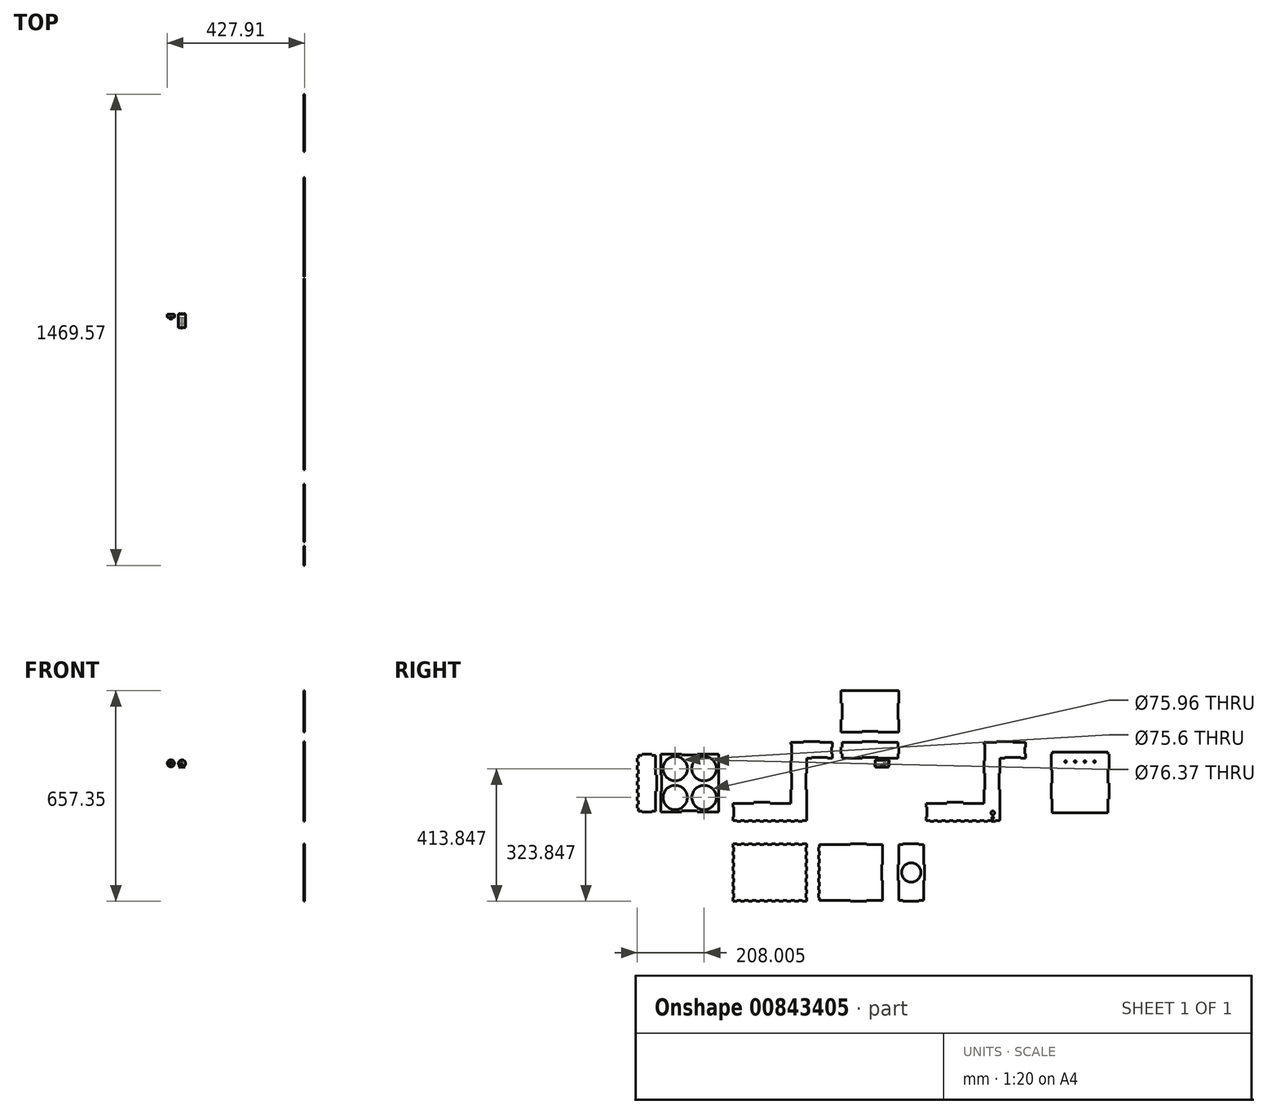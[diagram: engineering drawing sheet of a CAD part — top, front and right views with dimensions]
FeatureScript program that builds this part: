
annotation { "Feature Type Name" : "Feature", "Feature Type Description" : "" }
export const myFeature = defineFeature(function(context is Context, id is Id, definition is map)
    precondition{}
    {
        {
            var Q0;
            Q0=qCreatedBy(makeId("Right.planeOp"),FACE);
            var sketch = newSketch(context, id + "F0", { "sketchPlane" : qUnion([Q0])});
            skLineSegment(sketch, "E0", {"start": v(-485.36, -317) * mm, "end": v(-485.36, -305) * mm});
            skLineSegment(sketch, "E1", {"start": v(-305.36, -263) * mm, "end": v(-370.36, -263) * mm});
            skLineSegment(sketch, "E2", {"start": v(-265.36, -73) * mm, "end": v(-265.36, -70) * mm});
            skLineSegment(sketch, "E3", {"start": v(-265.36, -70) * mm, "end": v(-215.36, -70) * mm});
            skLineSegment(sketch, "E4", {"start": v(-215.36, -70) * mm, "end": v(-215.36, -73) * mm});
            skPoint(sketch, "E5.visualSharp", {"position": v(-175.36, -73) * mm});
            skPoint(sketch, "E6.visualSharp", {"position": v(-175.36, -123) * mm});
            skLineSegment(sketch, "E7", {"start": v(-485.36, -263) * mm, "end": v(-420.36, -263) * mm});
            skLineSegment(sketch, "E8", {"start": v(-420.36, -263) * mm, "end": v(-420.36, -260) * mm});
            skLineSegment(sketch, "E9", {"start": v(-420.36, -260) * mm, "end": v(-370.36, -260) * mm});
            skLineSegment(sketch, "E10", {"start": v(-370.36, -260) * mm, "end": v(-370.36, -263) * mm});
            skLineSegment(sketch, "E11.trimOffspring", {"start": v(-420.36, -263) * mm, "end": v(-485.36, -263) * mm});
            skLineSegment(sketch, "E12", {"start": v(-175.36, -118) * mm, "end": v(-175.36, -123) * mm});
            skLineSegment(sketch, "E13.bottom", {"start": v(-530.36, -290) * mm, "end": v(-595.36, -290) * mm});
            skLineSegment(sketch, "E13.top", {"start": v(-530.36, -110) * mm, "end": v(-595.36, -110) * mm});
            skLineSegment(sketch, "E13.left", {"start": v(-530.36, -290) * mm, "end": v(-530.36, -110) * mm});
            skLineSegment(sketch, "E13.right", {"start": v(-710.36, -290) * mm, "end": v(-710.36, -225) * mm});
            skLineSegment(sketch, "E14", {"start": v(-530.36, -290) * mm, "end": v(-535.36, -290) * mm});
            skLineSegment(sketch, "E15", {"start": v(-589.84, -110) * mm, "end": v(-595.36, -110) * mm});
            skLineSegment(sketch, "E16", {"start": v(-710.36, -110) * mm, "end": v(-705.36, -110) * mm});
            skLineSegment(sketch, "E17", {"start": v(-710.36, -290) * mm, "end": v(-705.36, -290) * mm});
            skLineSegment(sketch, "E18", {"start": v(-710.36, -290) * mm, "end": v(-710.36, -285) * mm});
            skLineSegment(sketch, "E19", {"start": v(-530.36, -110) * mm, "end": v(-530.36, -115) * mm});
            skLineSegment(sketch, "E20", {"start": v(-530.36, -110) * mm, "end": v(-530.36, -200) * mm});
            skCircle(sketch, "E21", {"center": v(-575.36, -245) * mm, "radius": 37.98 * mm});
            skCircle(sketch, "E22", {"center": v(-665.36, -245) * mm, "radius": 37.78 * mm});
            skCircle(sketch, "E23", {"center": v(-665.36, -155) * mm, "radius": 37.8 * mm});
            skCircle(sketch, "E24", {"center": v(-575.36, -155) * mm, "radius": 38.18 * mm});
            skPoint(sketch, "E25.trimOffspring.end.orphan", {"position": v(-710.36, -200) * mm});
            skPoint(sketch, "E26.start.orphan", {"position": v(-620.36, -110) * mm});
            skPoint(sketch, "E27.trimOffspring.end.orphan", {"position": v(-705.36, -290) * mm});
            skPoint(sketch, "E28.trimOffspring.end.orphan", {"position": v(-530.36, -285) * mm});
            skLineSegment(sketch, "E29", {"start": v(-595.36, -110) * mm, "end": v(-595.36, -113) * mm});
            skLineSegment(sketch, "E30", {"start": v(-595.36, -113) * mm, "end": v(-645.36, -113) * mm});
            skLineSegment(sketch, "E31", {"start": v(-645.36, -113) * mm, "end": v(-645.36, -110) * mm});
            skLineSegment(sketch, "E32.trimOffspring", {"start": v(-645.36, -110) * mm, "end": v(-710.36, -110) * mm});
            skLineSegment(sketch, "E33", {"start": v(-710.36, -290) * mm, "end": v(-645.36, -290) * mm});
            skLineSegment(sketch, "E34", {"start": v(-645.36, -290) * mm, "end": v(-645.36, -287) * mm});
            skLineSegment(sketch, "E35", {"start": v(-645.36, -287) * mm, "end": v(-595.36, -287) * mm});
            skLineSegment(sketch, "E36", {"start": v(-595.36, -287) * mm, "end": v(-595.36, -290) * mm});
            skPoint(sketch, "E37.orphan", {"position": v(-620.36, -290) * mm});
            skLineSegment(sketch, "E38.trimOffspring", {"start": v(-645.36, -290) * mm, "end": v(-710.36, -290) * mm});
            skLineSegment(sketch, "E39", {"start": v(-710.36, -110) * mm, "end": v(-710.36, -175) * mm});
            skLineSegment(sketch, "E40", {"start": v(-710.36, -175) * mm, "end": v(-707.36, -175) * mm});
            skLineSegment(sketch, "E41", {"start": v(-707.36, -175) * mm, "end": v(-707.36, -225) * mm});
            skLineSegment(sketch, "E42", {"start": v(-707.36, -225) * mm, "end": v(-710.36, -225) * mm});
            skLineSegment(sketch, "E43.trimOffspring", {"start": v(-710.36, -175) * mm, "end": v(-710.36, -110) * mm});
            skLineSegment(sketch, "E44", {"start": v(-175.36, -123) * mm, "end": v(-175.36, -108) * mm});
            skLineSegment(sketch, "E45", {"start": v(-175.36, -108) * mm, "end": v(-178.36, -108) * mm});
            skLineSegment(sketch, "E46", {"start": v(-178.36, -108) * mm, "end": v(-178.36, -88) * mm});
            skLineSegment(sketch, "E47", {"start": v(-178.36, -88) * mm, "end": v(-175.36, -88) * mm});
            skLineSegment(sketch, "E48.trimOffspring", {"start": v(-175.36, -108) * mm, "end": v(-175.36, -118) * mm});
            skLineSegment(sketch, "E49.bottom", {"start": v(-485.36, -568.84) * mm, "end": v(-473.36, -568.84) * mm});
            skLineSegment(sketch, "E49.top", {"start": v(-485.36, -388.84) * mm, "end": v(-473.36, -388.84) * mm});
            skLineSegment(sketch, "E49.left", {"start": v(-485.36, -568.84) * mm, "end": v(-485.36, -556.84) * mm});
            skLineSegment(sketch, "E49.right", {"start": v(-255.36, -568.84) * mm, "end": v(-255.36, -556.84) * mm});
            skLineSegment(sketch, "E50", {"start": v(-485.36, -568.84) * mm, "end": v(-485.36, -562.84) * mm});
            skLineSegment(sketch, "E51", {"start": v(-485.36, -562.84) * mm, "end": v(-485.36, -556.84) * mm});
            skLineSegment(sketch, "E52", {"start": v(-485.36, -544.84) * mm, "end": v(-485.36, -538.84) * mm});
            skLineSegment(sketch, "E53", {"start": v(-485.36, -538.84) * mm, "end": v(-485.36, -532.84) * mm});
            skLineSegment(sketch, "E54", {"start": v(-485.36, -520.84) * mm, "end": v(-485.36, -514.84) * mm});
            skLineSegment(sketch, "E55", {"start": v(-485.36, -514.84) * mm, "end": v(-485.36, -508.84) * mm});
            skLineSegment(sketch, "E56", {"start": v(-485.36, -496.84) * mm, "end": v(-485.36, -490.84) * mm});
            skLineSegment(sketch, "E57", {"start": v(-485.36, -490.84) * mm, "end": v(-485.36, -484.84) * mm});
            skLineSegment(sketch, "E58", {"start": v(-485.36, -472.84) * mm, "end": v(-485.36, -466.84) * mm});
            skLineSegment(sketch, "E59", {"start": v(-485.36, -466.84) * mm, "end": v(-485.36, -460.84) * mm});
            skLineSegment(sketch, "E60", {"start": v(-485.36, -448.84) * mm, "end": v(-485.36, -442.84) * mm});
            skLineSegment(sketch, "E61", {"start": v(-485.36, -442.84) * mm, "end": v(-485.36, -436.84) * mm});
            skLineSegment(sketch, "E62", {"start": v(-485.36, -424.84) * mm, "end": v(-485.36, -418.84) * mm});
            skLineSegment(sketch, "E63", {"start": v(-485.36, -418.84) * mm, "end": v(-485.36, -412.84) * mm});
            skLineSegment(sketch, "E64", {"start": v(-485.36, -400.84) * mm, "end": v(-485.36, -394.84) * mm});
            skLineSegment(sketch, "E65", {"start": v(-485.36, -556.84) * mm, "end": v(-482.36, -556.84) * mm});
            skLineSegment(sketch, "E66", {"start": v(-482.36, -556.84) * mm, "end": v(-482.36, -544.84) * mm});
            skLineSegment(sketch, "E67", {"start": v(-482.36, -544.84) * mm, "end": v(-485.36, -544.84) * mm});
            skLineSegment(sketch, "E68", {"start": v(-485.36, -532.84) * mm, "end": v(-482.36, -532.84) * mm});
            skLineSegment(sketch, "E69", {"start": v(-482.36, -532.84) * mm, "end": v(-482.36, -520.84) * mm});
            skLineSegment(sketch, "E70", {"start": v(-482.36, -520.84) * mm, "end": v(-485.36, -520.84) * mm});
            skLineSegment(sketch, "E71", {"start": v(-485.36, -508.84) * mm, "end": v(-482.36, -508.84) * mm});
            skLineSegment(sketch, "E72", {"start": v(-482.36, -508.84) * mm, "end": v(-482.36, -496.84) * mm});
            skLineSegment(sketch, "E73", {"start": v(-482.36, -496.84) * mm, "end": v(-485.36, -496.84) * mm});
            skPoint(sketch, "E74.end.orphan", {"position": v(-482.36, -484.84) * mm});
            skLineSegment(sketch, "E75", {"start": v(-485.36, -484.84) * mm, "end": v(-482.36, -484.84) * mm});
            skLineSegment(sketch, "E76", {"start": v(-482.36, -484.84) * mm, "end": v(-482.36, -472.84) * mm});
            skLineSegment(sketch, "E77", {"start": v(-482.36, -472.84) * mm, "end": v(-485.36, -472.84) * mm});
            skLineSegment(sketch, "E78", {"start": v(-485.36, -460.84) * mm, "end": v(-482.36, -460.84) * mm});
            skLineSegment(sketch, "E79", {"start": v(-482.36, -460.84) * mm, "end": v(-482.36, -448.84) * mm});
            skLineSegment(sketch, "E80", {"start": v(-482.36, -448.84) * mm, "end": v(-485.36, -448.84) * mm});
            skLineSegment(sketch, "E81", {"start": v(-485.36, -436.84) * mm, "end": v(-482.36, -436.84) * mm});
            skLineSegment(sketch, "E82", {"start": v(-482.36, -436.84) * mm, "end": v(-482.36, -424.84) * mm});
            skLineSegment(sketch, "E83", {"start": v(-482.36, -424.84) * mm, "end": v(-485.36, -424.84) * mm});
            skLineSegment(sketch, "E84", {"start": v(-485.36, -412.84) * mm, "end": v(-482.36, -412.84) * mm});
            skLineSegment(sketch, "E85", {"start": v(-482.36, -412.84) * mm, "end": v(-482.36, -400.84) * mm});
            skLineSegment(sketch, "E86", {"start": v(-482.36, -400.84) * mm, "end": v(-485.36, -400.84) * mm});
            skLineSegment(sketch, "E87.trimOffspring", {"start": v(-485.36, -400.84) * mm, "end": v(-485.36, -388.84) * mm});
            skLineSegment(sketch, "E88.trimOffspring", {"start": v(-485.36, -424.84) * mm, "end": v(-485.36, -412.84) * mm});
            skLineSegment(sketch, "E89.trimOffspring", {"start": v(-485.36, -448.84) * mm, "end": v(-485.36, -436.84) * mm});
            skLineSegment(sketch, "E90.trimOffspring", {"start": v(-485.36, -472.84) * mm, "end": v(-485.36, -460.84) * mm});
            skLineSegment(sketch, "E91.trimOffspring", {"start": v(-485.36, -496.84) * mm, "end": v(-485.36, -484.84) * mm});
            skLineSegment(sketch, "E92.trimOffspring", {"start": v(-485.36, -520.84) * mm, "end": v(-485.36, -508.84) * mm});
            skLineSegment(sketch, "E93.trimOffspring", {"start": v(-485.36, -544.84) * mm, "end": v(-485.36, -532.84) * mm});
            skLineSegment(sketch, "E94", {"start": v(-461.36, -568.84) * mm, "end": v(-449.36, -568.84) * mm});
            skLineSegment(sketch, "E95", {"start": v(-437.36, -568.84) * mm, "end": v(-425.36, -568.84) * mm});
            skLineSegment(sketch, "E96", {"start": v(-413.36, -568.84) * mm, "end": v(-401.36, -568.84) * mm});
            skLineSegment(sketch, "E97", {"start": v(-389.36, -568.77) * mm, "end": v(-377.36, -568.84) * mm});
            skLineSegment(sketch, "E98", {"start": v(-365.36, -568.84) * mm, "end": v(-353.36, -568.84) * mm});
            skLineSegment(sketch, "E99", {"start": v(-341.36, -568.84) * mm, "end": v(-329.36, -568.84) * mm});
            skLineSegment(sketch, "E100", {"start": v(-317.36, -568.84) * mm, "end": v(-305.36, -568.84) * mm});
            skLineSegment(sketch, "E101", {"start": v(-293.36, -568.84) * mm, "end": v(-281.36, -568.84) * mm});
            skLineSegment(sketch, "E102", {"start": v(-269.36, -568.84) * mm, "end": v(-255.36, -568.84) * mm});
            skLineSegment(sketch, "E103", {"start": v(-255.36, -544.84) * mm, "end": v(-255.36, -532.84) * mm});
            skLineSegment(sketch, "E104", {"start": v(-255.36, -520.84) * mm, "end": v(-255.36, -508.84) * mm});
            skLineSegment(sketch, "E105", {"start": v(-255.36, -496.84) * mm, "end": v(-255.36, -484.84) * mm});
            skLineSegment(sketch, "E106", {"start": v(-255.36, -472.84) * mm, "end": v(-255.36, -460.84) * mm});
            skLineSegment(sketch, "E107", {"start": v(-255.36, -448.84) * mm, "end": v(-255.36, -436.84) * mm});
            skLineSegment(sketch, "E108", {"start": v(-255.36, -424.84) * mm, "end": v(-255.36, -412.84) * mm});
            skLineSegment(sketch, "E109", {"start": v(-255.36, -400.84) * mm, "end": v(-255.36, -388.84) * mm});
            skLineSegment(sketch, "E110", {"start": v(-255.36, -388.84) * mm, "end": v(-269.36, -388.84) * mm});
            skLineSegment(sketch, "E111", {"start": v(-281.36, -388.84) * mm, "end": v(-293.36, -388.84) * mm});
            skLineSegment(sketch, "E112", {"start": v(-305.36, -388.84) * mm, "end": v(-317.36, -388.84) * mm});
            skLineSegment(sketch, "E113", {"start": v(-329.36, -388.84) * mm, "end": v(-341.36, -388.84) * mm});
            skLineSegment(sketch, "E114", {"start": v(-353.36, -388.84) * mm, "end": v(-365.36, -388.84) * mm});
            skLineSegment(sketch, "E115", {"start": v(-377.36, -388.84) * mm, "end": v(-389.36, -388.84) * mm});
            skLineSegment(sketch, "E116", {"start": v(-401.36, -388.84) * mm, "end": v(-413.36, -388.84) * mm});
            skLineSegment(sketch, "E117", {"start": v(-425.36, -388.84) * mm, "end": v(-437.36, -388.84) * mm});
            skLineSegment(sketch, "E118", {"start": v(-449.36, -388.84) * mm, "end": v(-461.36, -388.84) * mm});
            skLineSegment(sketch, "E119", {"start": v(-255.36, -400.84) * mm, "end": v(-258.36, -400.84) * mm});
            skLineSegment(sketch, "E120", {"start": v(-258.36, -400.84) * mm, "end": v(-258.36, -412.84) * mm});
            skLineSegment(sketch, "E121", {"start": v(-258.36, -412.84) * mm, "end": v(-255.36, -412.84) * mm});
            skLineSegment(sketch, "E122", {"start": v(-255.36, -424.84) * mm, "end": v(-258.36, -424.84) * mm});
            skLineSegment(sketch, "E123", {"start": v(-258.36, -424.84) * mm, "end": v(-258.36, -436.84) * mm});
            skLineSegment(sketch, "E124", {"start": v(-258.36, -436.84) * mm, "end": v(-255.36, -436.84) * mm});
            skLineSegment(sketch, "E125", {"start": v(-255.36, -448.84) * mm, "end": v(-258.36, -448.84) * mm});
            skLineSegment(sketch, "E126", {"start": v(-258.36, -448.84) * mm, "end": v(-258.36, -460.84) * mm});
            skLineSegment(sketch, "E127", {"start": v(-258.36, -460.84) * mm, "end": v(-255.36, -460.84) * mm});
            skLineSegment(sketch, "E128", {"start": v(-255.36, -472.84) * mm, "end": v(-258.36, -472.84) * mm});
            skLineSegment(sketch, "E129", {"start": v(-258.36, -472.84) * mm, "end": v(-258.36, -484.84) * mm});
            skLineSegment(sketch, "E130", {"start": v(-258.36, -484.84) * mm, "end": v(-255.36, -484.84) * mm});
            skLineSegment(sketch, "E131", {"start": v(-255.36, -496.84) * mm, "end": v(-258.36, -496.84) * mm});
            skLineSegment(sketch, "E132", {"start": v(-258.36, -496.84) * mm, "end": v(-258.36, -508.84) * mm});
            skLineSegment(sketch, "E133", {"start": v(-258.36, -508.84) * mm, "end": v(-255.36, -508.84) * mm});
            skLineSegment(sketch, "E134", {"start": v(-255.36, -520.84) * mm, "end": v(-258.36, -520.84) * mm});
            skPoint(sketch, "E134.endSnap0", {"position": v(-258.36, -502.84) * mm});
            skLineSegment(sketch, "E135", {"start": v(-258.36, -520.84) * mm, "end": v(-258.36, -532.84) * mm});
            skLineSegment(sketch, "E136", {"start": v(-258.36, -532.84) * mm, "end": v(-255.36, -532.84) * mm});
            skLineSegment(sketch, "E137", {"start": v(-255.36, -544.84) * mm, "end": v(-258.36, -544.84) * mm});
            skLineSegment(sketch, "E138", {"start": v(-258.36, -544.84) * mm, "end": v(-258.36, -556.84) * mm});
            skLineSegment(sketch, "E139", {"start": v(-258.36, -556.84) * mm, "end": v(-255.36, -556.84) * mm});
            skLineSegment(sketch, "E140", {"start": v(-269.36, -568.84) * mm, "end": v(-269.36, -565.84) * mm});
            skLineSegment(sketch, "E141", {"start": v(-269.36, -565.84) * mm, "end": v(-281.36, -565.84) * mm});
            skLineSegment(sketch, "E142", {"start": v(-281.36, -565.84) * mm, "end": v(-281.36, -568.84) * mm});
            skLineSegment(sketch, "E143", {"start": v(-293.36, -568.84) * mm, "end": v(-293.36, -565.84) * mm});
            skLineSegment(sketch, "E144", {"start": v(-293.36, -565.84) * mm, "end": v(-305.36, -565.84) * mm});
            skLineSegment(sketch, "E145", {"start": v(-305.36, -565.84) * mm, "end": v(-305.36, -568.84) * mm});
            skLineSegment(sketch, "E146.top", {"start": v(-329.36, -565.84) * mm, "end": v(-317.36, -565.84) * mm});
            skLineSegment(sketch, "E146.left", {"start": v(-329.36, -568.84) * mm, "end": v(-329.36, -565.84) * mm});
            skLineSegment(sketch, "E146.right", {"start": v(-317.36, -568.84) * mm, "end": v(-317.36, -565.84) * mm});
            skLineSegment(sketch, "E147.top", {"start": v(-353.36, -565.84) * mm, "end": v(-341.36, -565.84) * mm});
            skLineSegment(sketch, "E147.left", {"start": v(-353.36, -568.84) * mm, "end": v(-353.36, -565.84) * mm});
            skLineSegment(sketch, "E147.right", {"start": v(-341.36, -568.84) * mm, "end": v(-341.36, -565.84) * mm});
            skLineSegment(sketch, "E148.top", {"start": v(-377.36, -565.84) * mm, "end": v(-365.36, -565.84) * mm});
            skLineSegment(sketch, "E148.left", {"start": v(-377.36, -568.84) * mm, "end": v(-377.36, -565.84) * mm});
            skLineSegment(sketch, "E148.right", {"start": v(-365.36, -568.84) * mm, "end": v(-365.36, -565.84) * mm});
            skLineSegment(sketch, "E149.top", {"start": v(-401.36, -565.84) * mm, "end": v(-389.36, -565.84) * mm});
            skLineSegment(sketch, "E149.left", {"start": v(-401.36, -568.84) * mm, "end": v(-401.36, -565.84) * mm});
            skLineSegment(sketch, "E149.right", {"start": v(-389.36, -568.84) * mm, "end": v(-389.36, -565.84) * mm});
            skLineSegment(sketch, "E150.top", {"start": v(-425.36, -565.84) * mm, "end": v(-413.36, -565.84) * mm});
            skLineSegment(sketch, "E150.left", {"start": v(-425.36, -568.84) * mm, "end": v(-425.36, -565.84) * mm});
            skLineSegment(sketch, "E150.right", {"start": v(-413.36, -568.84) * mm, "end": v(-413.36, -565.84) * mm});
            skLineSegment(sketch, "E151.top", {"start": v(-449.36, -565.84) * mm, "end": v(-437.36, -565.84) * mm});
            skLineSegment(sketch, "E151.left", {"start": v(-449.36, -568.84) * mm, "end": v(-449.36, -565.84) * mm});
            skLineSegment(sketch, "E151.right", {"start": v(-437.36, -568.84) * mm, "end": v(-437.36, -565.84) * mm});
            skLineSegment(sketch, "E152.top", {"start": v(-473.36, -565.84) * mm, "end": v(-461.36, -565.84) * mm});
            skLineSegment(sketch, "E152.left", {"start": v(-473.36, -568.84) * mm, "end": v(-473.36, -565.84) * mm});
            skLineSegment(sketch, "E152.right", {"start": v(-461.36, -568.84) * mm, "end": v(-461.36, -565.84) * mm});
            skLineSegment(sketch, "E153.top", {"start": v(-269.36, -391.84) * mm, "end": v(-281.36, -391.84) * mm});
            skLineSegment(sketch, "E153.left", {"start": v(-269.36, -388.84) * mm, "end": v(-269.36, -391.84) * mm});
            skLineSegment(sketch, "E153.right", {"start": v(-281.36, -388.84) * mm, "end": v(-281.36, -391.84) * mm});
            skLineSegment(sketch, "E154.top", {"start": v(-293.36, -391.84) * mm, "end": v(-305.36, -391.84) * mm});
            skLineSegment(sketch, "E154.left", {"start": v(-293.36, -388.84) * mm, "end": v(-293.36, -391.84) * mm});
            skLineSegment(sketch, "E154.right", {"start": v(-305.36, -388.84) * mm, "end": v(-305.36, -391.84) * mm});
            skLineSegment(sketch, "E155.top", {"start": v(-329.36, -391.84) * mm, "end": v(-317.36, -391.84) * mm});
            skLineSegment(sketch, "E155.left", {"start": v(-329.36, -388.84) * mm, "end": v(-329.36, -391.84) * mm});
            skLineSegment(sketch, "E155.right", {"start": v(-317.36, -388.84) * mm, "end": v(-317.36, -391.84) * mm});
            skLineSegment(sketch, "E156.top", {"start": v(-353.36, -391.84) * mm, "end": v(-341.36, -391.84) * mm});
            skLineSegment(sketch, "E156.left", {"start": v(-353.36, -388.84) * mm, "end": v(-353.36, -391.84) * mm});
            skLineSegment(sketch, "E156.right", {"start": v(-341.36, -388.84) * mm, "end": v(-341.36, -391.84) * mm});
            skLineSegment(sketch, "E157.top", {"start": v(-377.36, -391.84) * mm, "end": v(-365.36, -391.84) * mm});
            skLineSegment(sketch, "E157.left", {"start": v(-377.36, -388.84) * mm, "end": v(-377.36, -391.84) * mm});
            skLineSegment(sketch, "E157.right", {"start": v(-365.36, -388.84) * mm, "end": v(-365.36, -391.84) * mm});
            skLineSegment(sketch, "E158.top", {"start": v(-401.36, -391.84) * mm, "end": v(-389.36, -391.84) * mm});
            skLineSegment(sketch, "E158.left", {"start": v(-401.36, -388.84) * mm, "end": v(-401.36, -391.84) * mm});
            skLineSegment(sketch, "E158.right", {"start": v(-389.36, -388.84) * mm, "end": v(-389.36, -391.84) * mm});
            skPoint(sketch, "E159.oppositeSnap0", {"position": v(-323.36, -391.84) * mm});
            skLineSegment(sketch, "E159.top", {"start": v(-425.36, -391.84) * mm, "end": v(-413.36, -391.84) * mm});
            skLineSegment(sketch, "E159.left", {"start": v(-425.36, -388.84) * mm, "end": v(-425.36, -391.84) * mm});
            skLineSegment(sketch, "E159.right", {"start": v(-413.36, -388.84) * mm, "end": v(-413.36, -391.84) * mm});
            skLineSegment(sketch, "E160.top", {"start": v(-449.36, -391.84) * mm, "end": v(-437.36, -391.84) * mm});
            skLineSegment(sketch, "E160.left", {"start": v(-449.36, -388.84) * mm, "end": v(-449.36, -391.84) * mm});
            skLineSegment(sketch, "E160.right", {"start": v(-437.36, -388.84) * mm, "end": v(-437.36, -391.84) * mm});
            skLineSegment(sketch, "E161.bottom", {"start": v(-461.36, -388.84) * mm, "end": v(-460, -388.84) * mm});
            skLineSegment(sketch, "E161.top", {"start": v(-473.36, -392.25) * mm, "end": v(-460, -392.25) * mm});
            skLineSegment(sketch, "E161.left", {"start": v(-473.36, -388.84) * mm, "end": v(-473.36, -392.25) * mm});
            skLineSegment(sketch, "E161.right", {"start": v(-460, -388.84) * mm, "end": v(-460, -392.25) * mm});
            skLineSegment(sketch, "E162.right", {"start": v(-425.66, -320) * mm, "end": v(-425.66, -320) * mm});
            skLineSegment(sketch, "E163.bottom", {"start": v(-425.66, -320) * mm, "end": v(-413.66, -320) * mm});
            skLineSegment(sketch, "E164.top", {"start": v(-413.66, -317) * mm, "end": v(-401.66, -317) * mm});
            skLineSegment(sketch, "E164.left", {"start": v(-413.66, -320) * mm, "end": v(-413.66, -317) * mm});
            skLineSegment(sketch, "E164.right", {"start": v(-401.66, -320) * mm, "end": v(-401.66, -317) * mm});
            skLineSegment(sketch, "E165.top", {"start": v(-389.66, -317) * mm, "end": v(-377.66, -317) * mm});
            skLineSegment(sketch, "E165.left", {"start": v(-389.66, -320) * mm, "end": v(-389.66, -317) * mm});
            skLineSegment(sketch, "E165.right", {"start": v(-377.66, -320) * mm, "end": v(-377.66, -317) * mm});
            skLineSegment(sketch, "E166.top", {"start": v(-365.66, -317) * mm, "end": v(-353.66, -317) * mm});
            skLineSegment(sketch, "E166.left", {"start": v(-365.66, -320) * mm, "end": v(-365.66, -317) * mm});
            skLineSegment(sketch, "E166.right", {"start": v(-353.66, -320) * mm, "end": v(-353.66, -317) * mm});
            skLineSegment(sketch, "E167.bottom", {"start": v(-353.66, -320) * mm, "end": v(-341.66, -320) * mm});
            skLineSegment(sketch, "E167.top", {"start": v(-353.36, -320) * mm, "end": v(-341.66, -320) * mm});
            skLineSegment(sketch, "E168.top", {"start": v(-341.66, -317) * mm, "end": v(-329.66, -317) * mm});
            skLineSegment(sketch, "E168.left", {"start": v(-341.66, -320) * mm, "end": v(-341.66, -317) * mm});
            skLineSegment(sketch, "E168.right", {"start": v(-329.66, -320) * mm, "end": v(-329.66, -317) * mm});
            skLineSegment(sketch, "E169.bottom", {"start": v(-329.66, -320) * mm, "end": v(-317.66, -320) * mm});
            skLineSegment(sketch, "E169.top", {"start": v(-329.36, -320) * mm, "end": v(-317.66, -320) * mm});
            skLineSegment(sketch, "E170.top", {"start": v(-317.66, -317) * mm, "end": v(-305.66, -317) * mm});
            skLineSegment(sketch, "E170.left", {"start": v(-317.66, -320) * mm, "end": v(-317.66, -317) * mm});
            skLineSegment(sketch, "E170.right", {"start": v(-305.66, -320) * mm, "end": v(-305.66, -317) * mm});
            skLineSegment(sketch, "E171.trimOffspring", {"start": v(-389.36, -568.84) * mm, "end": v(-377.36, -568.84) * mm});
            skLineSegment(sketch, "E172.trimOffspring", {"start": v(-461.36, -388.84) * mm, "end": v(-449.36, -388.84) * mm});
            skLineSegment(sketch, "E173.trimOffspring", {"start": v(-437.36, -388.84) * mm, "end": v(-425.36, -388.84) * mm});
            skLineSegment(sketch, "E174.trimOffspring", {"start": v(-413.36, -388.84) * mm, "end": v(-401.36, -388.84) * mm});
            skLineSegment(sketch, "E175.trimOffspring", {"start": v(-389.36, -388.84) * mm, "end": v(-377.36, -388.84) * mm});
            skLineSegment(sketch, "E176.trimOffspring", {"start": v(-365.36, -388.84) * mm, "end": v(-353.36, -388.84) * mm});
            skLineSegment(sketch, "E177.trimOffspring", {"start": v(-341.36, -388.84) * mm, "end": v(-329.36, -388.84) * mm});
            skLineSegment(sketch, "E178.trimOffspring", {"start": v(-317.36, -388.84) * mm, "end": v(-305.36, -388.84) * mm});
            skLineSegment(sketch, "E179.trimOffspring", {"start": v(-293.36, -388.84) * mm, "end": v(-281.36, -388.84) * mm});
            skLineSegment(sketch, "E180.trimOffspring", {"start": v(-269.36, -388.84) * mm, "end": v(-255.36, -388.84) * mm});
            skLineSegment(sketch, "E181.trimOffspring", {"start": v(-341.66, -320) * mm, "end": v(-353.66, -320) * mm});
            skLineSegment(sketch, "E182.trimOffspring", {"start": v(-389.66, -320) * mm, "end": v(-401.66, -320) * mm});
            skLineSegment(sketch, "E183.bottom", {"start": v(-302.36, -220) * mm, "end": v(-305.36, -220) * mm});
            skLineSegment(sketch, "E184.bottom", {"start": v(-302.36, -130) * mm, "end": v(-302.36, -130) * mm});
            skPoint(sketch, "E185", {"position": v(-305.36, -263) * mm});
            skLineSegment(sketch, "E186", {"start": v(-305.36, -170) * mm, "end": v(-302.36, -170) * mm});
            skLineSegment(sketch, "E187.bottom", {"start": v(-485.36, -275) * mm, "end": v(-482.37, -275) * mm});
            skLineSegment(sketch, "E187.top", {"start": v(-485.36, -305) * mm, "end": v(-482.37, -305) * mm});
            skLineSegment(sketch, "E187.right", {"start": v(-482.37, -275) * mm, "end": v(-482.37, -305) * mm});
            skLineSegment(sketch, "E188.trimOffspring", {"start": v(-485.36, -275) * mm, "end": v(-485.36, -263) * mm});
            skLineSegment(sketch, "E189", {"start": v(-305.36, -263) * mm, "end": v(-305.36, -220) * mm});
            skLineSegment(sketch, "E190.right", {"start": v(-726.36, -284.7) * mm, "end": v(-726.36, -225.2) * mm});
            skLineSegment(sketch, "E191", {"start": v(-726.36, -113.2) * mm, "end": v(-726.36, -175.2) * mm});
            skLineSegment(sketch, "E192", {"start": v(-726.36, -175.2) * mm, "end": v(-723.36, -175.2) * mm});
            skLineSegment(sketch, "E193", {"start": v(-723.36, -175.2) * mm, "end": v(-723.36, -225.2) * mm});
            skLineSegment(sketch, "E194", {"start": v(-723.36, -225.2) * mm, "end": v(-726.36, -225.2) * mm});
            skLineSegment(sketch, "E195.trimOffspring", {"start": v(-726.36, -175.2) * mm, "end": v(-726.36, -113.2) * mm});
            skLineSegment(sketch, "E196.bottom", {"start": v(-425.66, -317) * mm, "end": v(-437.36, -317) * mm});
            skLineSegment(sketch, "E196.top", {"start": v(-413.66, -320) * mm, "end": v(-425.66, -320) * mm});
            skLineSegment(sketch, "E196.left", {"start": v(-413.66, -317) * mm, "end": v(-413.66, -320) * mm});
            skLineSegment(sketch, "E197", {"start": v(-425.66, -320) * mm, "end": v(-425.66, -317) * mm});
            skLineSegment(sketch, "E198", {"start": v(-437.36, -320) * mm, "end": v(-437.36, -317) * mm});
            skLineSegment(sketch, "E199", {"start": v(-449.36, -320) * mm, "end": v(-449.36, -317) * mm});
            skLineSegment(sketch, "E200", {"start": v(-461.36, -320) * mm, "end": v(-461.36, -317) * mm});
            skLineSegment(sketch, "E201", {"start": v(-473.36, -320) * mm, "end": v(-473.36, -317) * mm});
            skLineSegment(sketch, "E202.trimOffspring", {"start": v(-437.36, -320) * mm, "end": v(-449.36, -320) * mm});
            skLineSegment(sketch, "E203.trimOffspring", {"start": v(-449.36, -317) * mm, "end": v(-461.36, -317) * mm});
            skLineSegment(sketch, "E204.trimOffspring", {"start": v(-461.36, -320) * mm, "end": v(-473.36, -320) * mm});
            skLineSegment(sketch, "E205.trimOffspring", {"start": v(-473.36, -317) * mm, "end": v(-485.36, -317) * mm});
            skLineSegment(sketch, "E206", {"start": v(-302.36, -220) * mm, "end": v(-302.36, -170) * mm});
            skPoint(sketch, "E183.top.end.orphan", {"position": v(-299.56, -200) * mm});
            skLineSegment(sketch, "E207", {"start": v(-305.36, -170) * mm, "end": v(-305.36, -130) * mm});
            skLineSegment(sketch, "E208", {"start": v(-302.36, -130) * mm, "end": v(-305.36, -130) * mm});
            skLineSegment(sketch, "E209", {"start": v(-302.36, -130) * mm, "end": v(-302.36, -80) * mm});
            skLineSegment(sketch, "E210", {"start": v(-302.36, -80) * mm, "end": v(-305.36, -80) * mm});
            skLineSegment(sketch, "E211.trimOffspring", {"start": v(-305.36, -80) * mm, "end": v(-305.36, -73) * mm});
            skLineSegment(sketch, "E212", {"start": v(-305.36, -73) * mm, "end": v(-265.36, -73) * mm});
            skLineSegment(sketch, "E213", {"start": v(-215.36, -73) * mm, "end": v(-175.36, -73) * mm});
            skLineSegment(sketch, "E214", {"start": v(-240.36, -123) * mm, "end": v(-240.36, -120) * mm});
            skLineSegment(sketch, "E215", {"start": v(-240.36, -120) * mm, "end": v(-190.36, -120) * mm});
            skLineSegment(sketch, "E216", {"start": v(-190.36, -120) * mm, "end": v(-190.36, -123) * mm});
            skLineSegment(sketch, "E217.trimOffspring", {"start": v(-240.36, -123) * mm, "end": v(-255.36, -123) * mm});
            skLineSegment(sketch, "E218", {"start": v(-175.36, -123) * mm, "end": v(-190.36, -123) * mm});
            skLineSegment(sketch, "E219", {"start": v(-175.36, -73) * mm, "end": v(-175.36, -88) * mm});
            skLineSegment(sketch, "E220", {"start": v(-377.66, -320) * mm, "end": v(-365.66, -320) * mm});
            skLineSegment(sketch, "E221", {"start": v(-255.36, -484.84) * mm, "end": v(-255.36, -484.84) * mm});
            skLineSegment(sketch, "E222", {"start": v(-255.36, -123) * mm, "end": v(-255.36, -170) * mm});
            skLineSegment(sketch, "E223.bottom", {"start": v(-255.36, -220) * mm, "end": v(-258.36, -220) * mm});
            skLineSegment(sketch, "E223.top", {"start": v(-255.36, -170) * mm, "end": v(-258.36, -170) * mm});
            skLineSegment(sketch, "E223.right", {"start": v(-258.36, -220) * mm, "end": v(-258.36, -170) * mm});
            skLineSegment(sketch, "E224.trimOffspring", {"start": v(-255.36, -220) * mm, "end": v(-255.36, -287) * mm});
            skLineSegment(sketch, "E225.MirrorCS", {"start": v(-281.66, -320) * mm, "end": v(-281.66, -317) * mm});
            skLineSegment(sketch, "E226.MirrorCS", {"start": v(-293.66, -320) * mm, "end": v(-293.66, -317) * mm});
            skLineSegment(sketch, "E227", {"start": v(-305.66, -320) * mm, "end": v(-293.66, -320) * mm});
            skLineSegment(sketch, "E228", {"start": v(-293.66, -317) * mm, "end": v(-281.66, -317) * mm});
            skLineSegment(sketch, "E229", {"start": v(-281.66, -320) * mm, "end": v(-269.66, -320) * mm});
            skLineSegment(sketch, "E230.left", {"start": v(-269.66, -320) * mm, "end": v(-269.66, -317) * mm});
            skLineSegment(sketch, "E231.MirrorCS", {"start": v(28.62, -73) * mm, "end": v(28.62, -88) * mm});
            skLineSegment(sketch, "E232.MirrorCS", {"start": v(31.62, -88) * mm, "end": v(28.62, -88) * mm});
            skPoint(sketch, "E233.MirrorP", {"position": v(28.62, -73) * mm});
            skPoint(sketch, "E234.visualSharp", {"position": v(-145.38, -73) * mm});
            skPoint(sketch, "E235.visualSharp", {"position": v(-145.38, -123) * mm});
            skLineSegment(sketch, "E236", {"start": v(-145.38, -118) * mm, "end": v(-145.38, -123) * mm});
            skLineSegment(sketch, "E237", {"start": v(-145.38, -123) * mm, "end": v(-145.38, -108) * mm});
            skLineSegment(sketch, "E238", {"start": v(-145.38, -108) * mm, "end": v(-148.38, -108) * mm});
            skLineSegment(sketch, "E239", {"start": v(-148.38, -108) * mm, "end": v(-148.38, -88) * mm});
            skLineSegment(sketch, "E240", {"start": v(-148.38, -88) * mm, "end": v(-145.38, -88) * mm});
            skLineSegment(sketch, "E241.trimOffspring", {"start": v(-145.38, -108) * mm, "end": v(-145.38, -118) * mm});
            skLineSegment(sketch, "E242", {"start": v(-145.38, -73) * mm, "end": v(-145.38, -88) * mm});
            skLineSegment(sketch, "E243", {"start": v(-145.38, -73) * mm, "end": v(-83.38, -73) * mm});
            skLineSegment(sketch, "E244", {"start": v(31.62, -88) * mm, "end": v(31.62, -108) * mm});
            skLineSegment(sketch, "E245", {"start": v(31.62, -108) * mm, "end": v(28.62, -108) * mm});
            skLineSegment(sketch, "E246", {"start": v(28.62, -108) * mm, "end": v(28.62, -123) * mm});
            skLineSegment(sketch, "E247", {"start": v(28.62, -123) * mm, "end": v(-33.38, -123) * mm});
            skLineSegment(sketch, "E248.top", {"start": v(-83.38, -70) * mm, "end": v(-33.38, -70) * mm});
            skLineSegment(sketch, "E249.trimOffspring", {"start": v(-33.38, -73) * mm, "end": v(28.62, -73) * mm});
            skLineSegment(sketch, "E250.top", {"start": v(-148.38, 88.5) * mm, "end": v(31.62, 88.5) * mm});
            skLineSegment(sketch, "E250.left", {"start": v(-148.38, -41.5) * mm, "end": v(-148.38, -1.5) * mm});
            skLineSegment(sketch, "E251.bottom", {"start": v(-83.38, -38.5) * mm, "end": v(-33.38, -38.5) * mm});
            skLineSegment(sketch, "E252", {"start": v(-33.38, -41.5) * mm, "end": v(31.62, -41.5) * mm});
            skLineSegment(sketch, "E253", {"start": v(-83.38, -41.5) * mm, "end": v(-148.38, -41.5) * mm});
            skLineSegment(sketch, "E254.bottom", {"start": v(-148.38, 48.5) * mm, "end": v(-145.38, 48.5) * mm});
            skLineSegment(sketch, "E254.top", {"start": v(-148.38, -1.5) * mm, "end": v(-145.38, -1.5) * mm});
            skLineSegment(sketch, "E254.right", {"start": v(-145.38, 48.5) * mm, "end": v(-145.38, -1.5) * mm});
            skLineSegment(sketch, "E255.bottom", {"start": v(31.62, 48.5) * mm, "end": v(28.62, 48.5) * mm});
            skLineSegment(sketch, "E255.top", {"start": v(31.62, -1.5) * mm, "end": v(28.62, -1.5) * mm});
            skLineSegment(sketch, "E255.right", {"start": v(28.62, 48.5) * mm, "end": v(28.62, -1.5) * mm});
            skLineSegment(sketch, "E256.trimOffspring", {"start": v(-148.38, 48.5) * mm, "end": v(-148.38, 88.5) * mm});
            skLineSegment(sketch, "E257.trimOffspring", {"start": v(31.62, 48.5) * mm, "end": v(31.62, 88.5) * mm});
            skLineSegment(sketch, "E258", {"start": v(31.62, -41.5) * mm, "end": v(31.62, -1.5) * mm});
            skPoint(sketch, "E259.orphan", {"position": v(31.62, -123) * mm});
            skLineSegment(sketch, "E260", {"start": v(-83.38, -38.5) * mm, "end": v(-83.38, -41.5) * mm});
            skLineSegment(sketch, "E261", {"start": v(-33.38, -38.5) * mm, "end": v(-33.38, -41.5) * mm});
            skLineSegment(sketch, "E262", {"start": v(-83.38, -73) * mm, "end": v(-83.38, -70) * mm});
            skLineSegment(sketch, "E263", {"start": v(-33.38, -73) * mm, "end": v(-33.38, -70) * mm});
            skLineSegment(sketch, "E264.top", {"start": v(-83.38, -120) * mm, "end": v(-33.38, -120) * mm});
            skLineSegment(sketch, "E264.left", {"start": v(-83.38, -123) * mm, "end": v(-83.38, -120) * mm});
            skLineSegment(sketch, "E264.right", {"start": v(-33.38, -123) * mm, "end": v(-33.38, -120) * mm});
            skLineSegment(sketch, "E265.trimOffspring", {"start": v(-83.38, -123) * mm, "end": v(-145.38, -123) * mm});
            skLineSegment(sketch, "E266.MirrorCS", {"start": v(509.07, -200) * mm, "end": v(506.07, -200) * mm});
            skLineSegment(sketch, "E267.MirrorCS", {"start": v(506.21, -250) * mm, "end": v(509.21, -250) * mm});
            skLineSegment(sketch, "E268.MirrorCS", {"start": v(506.07, -110) * mm, "end": v(509.07, -110) * mm});
            skLineSegment(sketch, "E269.MirrorCS", {"start": v(509.07, -200) * mm, "end": v(509.07, -160) * mm});
            skLineSegment(sketch, "E270.MirrorCS", {"start": v(506.21, -250) * mm, "end": v(506.21, -200) * mm});
            skLineSegment(sketch, "E271.MirrorCS", {"start": v(506.07, -160) * mm, "end": v(506.07, -110) * mm});
            skLineSegment(sketch, "E272.MirrorCS", {"start": v(509.21, -293) * mm, "end": v(509.21, -250) * mm});
            skPoint(sketch, "E273.MirrorP", {"position": v(509.21, -293) * mm});
            skLineSegment(sketch, "E274", {"start": v(509.14, -103) * mm, "end": v(509.07, -110) * mm});
            skLineSegment(sketch, "E275.MirrorCS", {"start": v(686.21, -110) * mm, "end": v(683.21, -110) * mm});
            skLineSegment(sketch, "E276.MirrorCS", {"start": v(686.21, -250) * mm, "end": v(683.21, -250) * mm});
            skLineSegment(sketch, "E277.MirrorCS", {"start": v(683.21, -293) * mm, "end": v(683.21, -250) * mm});
            skPoint(sketch, "E278.MirrorP", {"position": v(683.21, -293) * mm});
            skLineSegment(sketch, "E279.MirrorCS", {"start": v(686.21, -160) * mm, "end": v(686.21, -110) * mm});
            skLineSegment(sketch, "E280.MirrorCS", {"start": v(686.21, -250) * mm, "end": v(686.21, -200) * mm});
            skLineSegment(sketch, "E281.MirrorCS", {"start": v(683.21, -200) * mm, "end": v(683.21, -160) * mm});
            skLineSegment(sketch, "E282.MirrorCS", {"start": v(683.14, -103) * mm, "end": v(683.21, -110) * mm});
            skLineSegment(sketch, "E283", {"start": v(509.21, -293) * mm, "end": v(683.21, -293) * mm});
            skLineSegment(sketch, "E284", {"start": v(509.14, -103) * mm, "end": v(683.14, -103) * mm});
            skLineSegment(sketch, "E285", {"start": v(-255.36, -287) * mm, "end": v(-255.36, -317) * mm});
            skLineSegment(sketch, "E286", {"start": v(-255.36, -317) * mm, "end": v(-269.66, -317) * mm});
            skLineSegment(sketch, "E287", {"start": v(116.62, -317) * mm, "end": v(116.62, -305) * mm});
            skLineSegment(sketch, "E288", {"start": v(296.62, -263) * mm, "end": v(231.62, -263) * mm});
            skCircle(sketch, "E289", {"center": v(324.22, -293) * mm, "radius": 6 * mm});
            skCircle(sketch, "E290", {"center": v(324.22, -308.46) * mm, "radius": 3 * mm});
            skLineSegment(sketch, "E291", {"start": v(336.62, -73) * mm, "end": v(336.62, -70) * mm});
            skLineSegment(sketch, "E292", {"start": v(336.62, -70) * mm, "end": v(386.62, -70) * mm});
            skLineSegment(sketch, "E293", {"start": v(386.62, -70) * mm, "end": v(386.62, -73) * mm});
            skPoint(sketch, "E294.visualSharp", {"position": v(426.62, -73) * mm});
            skPoint(sketch, "E295.visualSharp", {"position": v(426.62, -123) * mm});
            skLineSegment(sketch, "E296", {"start": v(116.62, -263) * mm, "end": v(181.62, -263) * mm});
            skLineSegment(sketch, "E297", {"start": v(181.62, -263) * mm, "end": v(181.62, -260) * mm});
            skLineSegment(sketch, "E298", {"start": v(181.62, -260) * mm, "end": v(231.62, -260) * mm});
            skLineSegment(sketch, "E299", {"start": v(231.62, -260) * mm, "end": v(231.62, -263) * mm});
            skLineSegment(sketch, "E300.trimOffspring", {"start": v(181.62, -263) * mm, "end": v(116.62, -263) * mm});
            skLineSegment(sketch, "E301", {"start": v(426.62, -118) * mm, "end": v(426.62, -123) * mm});
            skLineSegment(sketch, "E302", {"start": v(426.62, -123) * mm, "end": v(426.62, -108) * mm});
            skLineSegment(sketch, "E303", {"start": v(426.62, -108) * mm, "end": v(423.62, -108) * mm});
            skLineSegment(sketch, "E304", {"start": v(423.62, -108) * mm, "end": v(423.62, -88) * mm});
            skLineSegment(sketch, "E305", {"start": v(423.62, -88) * mm, "end": v(426.62, -88) * mm});
            skLineSegment(sketch, "E306.trimOffspring", {"start": v(426.62, -108) * mm, "end": v(426.62, -118) * mm});
            skLineSegment(sketch, "E307.right", {"start": v(-600.35, -417.36) * mm, "end": v(-600.35, -417.36) * mm});
            skLineSegment(sketch, "E308.bottom", {"start": v(176.31, -320) * mm, "end": v(188.31, -320) * mm});
            skLineSegment(sketch, "E309.top", {"start": v(188.31, -317) * mm, "end": v(200.31, -317) * mm});
            skLineSegment(sketch, "E309.left", {"start": v(188.31, -320) * mm, "end": v(188.31, -317) * mm});
            skLineSegment(sketch, "E309.right", {"start": v(200.31, -320) * mm, "end": v(200.31, -317) * mm});
            skLineSegment(sketch, "E310.top", {"start": v(212.31, -317) * mm, "end": v(224.31, -317) * mm});
            skLineSegment(sketch, "E310.left", {"start": v(212.31, -320) * mm, "end": v(212.31, -317) * mm});
            skLineSegment(sketch, "E310.right", {"start": v(224.31, -320) * mm, "end": v(224.31, -317) * mm});
            skLineSegment(sketch, "E311.top", {"start": v(236.31, -317) * mm, "end": v(248.31, -317) * mm});
            skLineSegment(sketch, "E311.left", {"start": v(236.31, -320) * mm, "end": v(236.31, -317) * mm});
            skLineSegment(sketch, "E311.right", {"start": v(248.31, -320) * mm, "end": v(248.31, -317) * mm});
            skLineSegment(sketch, "E312.bottom", {"start": v(248.31, -320) * mm, "end": v(260.31, -320) * mm});
            skLineSegment(sketch, "E312.top", {"start": v(248.62, -320) * mm, "end": v(260.31, -320) * mm});
            skLineSegment(sketch, "E313.top", {"start": v(260.31, -317) * mm, "end": v(272.31, -317) * mm});
            skLineSegment(sketch, "E313.left", {"start": v(260.31, -320) * mm, "end": v(260.31, -317) * mm});
            skLineSegment(sketch, "E313.right", {"start": v(272.31, -320) * mm, "end": v(272.31, -317) * mm});
            skLineSegment(sketch, "E314.bottom", {"start": v(272.31, -320) * mm, "end": v(284.31, -320) * mm});
            skLineSegment(sketch, "E314.top", {"start": v(272.62, -320) * mm, "end": v(284.31, -320) * mm});
            skLineSegment(sketch, "E315.top", {"start": v(284.31, -317) * mm, "end": v(296.31, -317) * mm});
            skLineSegment(sketch, "E315.left", {"start": v(284.31, -320) * mm, "end": v(284.31, -317) * mm});
            skLineSegment(sketch, "E315.right", {"start": v(296.31, -320) * mm, "end": v(296.31, -317) * mm});
            skLineSegment(sketch, "E316.trimOffspring", {"start": v(260.31, -320) * mm, "end": v(248.31, -320) * mm});
            skLineSegment(sketch, "E317.trimOffspring", {"start": v(212.31, -320) * mm, "end": v(200.31, -320) * mm});
            skLineSegment(sketch, "E318.bottom", {"start": v(299.62, -220) * mm, "end": v(296.62, -220) * mm});
            skLineSegment(sketch, "E319.bottom", {"start": v(-477.04, -227.36) * mm, "end": v(-477.04, -227.36) * mm});
            skPoint(sketch, "E320", {"position": v(296.62, -263) * mm});
            skLineSegment(sketch, "E321", {"start": v(296.62, -170) * mm, "end": v(299.62, -170) * mm});
            skLineSegment(sketch, "E322.bottom", {"start": v(116.62, -275) * mm, "end": v(119.6, -275) * mm});
            skLineSegment(sketch, "E322.top", {"start": v(116.62, -305) * mm, "end": v(119.6, -305) * mm});
            skLineSegment(sketch, "E322.right", {"start": v(119.6, -275) * mm, "end": v(119.6, -305) * mm});
            skLineSegment(sketch, "E323.trimOffspring", {"start": v(116.62, -275) * mm, "end": v(116.62, -263) * mm});
            skLineSegment(sketch, "E324", {"start": v(296.62, -263) * mm, "end": v(296.62, -220) * mm});
            skLineSegment(sketch, "E325.bottom", {"start": v(176.31, -317) * mm, "end": v(164.62, -317) * mm});
            skLineSegment(sketch, "E325.top", {"start": v(188.31, -320) * mm, "end": v(176.31, -320) * mm});
            skLineSegment(sketch, "E325.left", {"start": v(188.31, -317) * mm, "end": v(188.31, -320) * mm});
            skLineSegment(sketch, "E326", {"start": v(176.31, -320) * mm, "end": v(176.31, -317) * mm});
            skLineSegment(sketch, "E327", {"start": v(164.62, -320) * mm, "end": v(164.62, -317) * mm});
            skLineSegment(sketch, "E328", {"start": v(152.62, -320) * mm, "end": v(152.62, -317) * mm});
            skLineSegment(sketch, "E329", {"start": v(140.62, -320) * mm, "end": v(140.62, -317) * mm});
            skLineSegment(sketch, "E330", {"start": v(128.62, -320) * mm, "end": v(128.62, -317) * mm});
            skLineSegment(sketch, "E331.trimOffspring", {"start": v(164.62, -320) * mm, "end": v(152.62, -320) * mm});
            skLineSegment(sketch, "E332.trimOffspring", {"start": v(152.62, -317) * mm, "end": v(140.62, -317) * mm});
            skLineSegment(sketch, "E333.trimOffspring", {"start": v(140.62, -320) * mm, "end": v(128.62, -320) * mm});
            skLineSegment(sketch, "E334.trimOffspring", {"start": v(128.62, -317) * mm, "end": v(116.62, -317) * mm});
            skLineSegment(sketch, "E335", {"start": v(299.62, -220) * mm, "end": v(299.62, -170) * mm});
            skPoint(sketch, "E318.top.end.orphan", {"position": v(302.41, -200) * mm});
            skLineSegment(sketch, "E336", {"start": v(296.62, -170) * mm, "end": v(296.62, -130) * mm});
            skLineSegment(sketch, "E337", {"start": v(299.62, -130) * mm, "end": v(296.62, -130) * mm});
            skLineSegment(sketch, "E338", {"start": v(299.62, -130) * mm, "end": v(299.62, -80) * mm});
            skLineSegment(sketch, "E339", {"start": v(299.62, -80) * mm, "end": v(296.62, -80) * mm});
            skLineSegment(sketch, "E340.trimOffspring", {"start": v(296.62, -80) * mm, "end": v(296.62, -73) * mm});
            skLineSegment(sketch, "E341", {"start": v(296.62, -73) * mm, "end": v(336.62, -73) * mm});
            skLineSegment(sketch, "E342", {"start": v(386.62, -73) * mm, "end": v(426.62, -73) * mm});
            skLineSegment(sketch, "E343", {"start": v(361.62, -123) * mm, "end": v(361.62, -120) * mm});
            skLineSegment(sketch, "E344", {"start": v(361.62, -120) * mm, "end": v(411.62, -120) * mm});
            skLineSegment(sketch, "E345", {"start": v(411.62, -120) * mm, "end": v(411.62, -123) * mm});
            skLineSegment(sketch, "E346.trimOffspring", {"start": v(361.62, -123) * mm, "end": v(346.62, -123) * mm});
            skLineSegment(sketch, "E347", {"start": v(426.62, -123) * mm, "end": v(411.62, -123) * mm});
            skLineSegment(sketch, "E348", {"start": v(426.62, -73) * mm, "end": v(426.62, -88) * mm});
            skLineSegment(sketch, "E349", {"start": v(224.31, -320) * mm, "end": v(236.31, -320) * mm});
            skLineSegment(sketch, "E350", {"start": v(346.62, -123) * mm, "end": v(346.62, -170) * mm});
            skLineSegment(sketch, "E351.bottom", {"start": v(346.62, -220) * mm, "end": v(343.62, -220) * mm});
            skLineSegment(sketch, "E351.top", {"start": v(346.62, -170) * mm, "end": v(343.62, -170) * mm});
            skLineSegment(sketch, "E351.right", {"start": v(343.62, -220) * mm, "end": v(343.62, -170) * mm});
            skLineSegment(sketch, "E352.trimOffspring", {"start": v(346.62, -220) * mm, "end": v(346.62, -287) * mm});
            skLineSegment(sketch, "E353.MirrorCS", {"start": v(320.31, -320) * mm, "end": v(320.31, -317) * mm});
            skLineSegment(sketch, "E354.MirrorCS", {"start": v(308.31, -320) * mm, "end": v(308.31, -317) * mm});
            skLineSegment(sketch, "E355", {"start": v(296.31, -320) * mm, "end": v(308.31, -320) * mm});
            skLineSegment(sketch, "E356", {"start": v(308.31, -317) * mm, "end": v(320.31, -317) * mm});
            skLineSegment(sketch, "E357", {"start": v(320.31, -320) * mm, "end": v(332.31, -320) * mm});
            skLineSegment(sketch, "E358.left", {"start": v(332.31, -320) * mm, "end": v(332.31, -317) * mm});
            skLineSegment(sketch, "E359", {"start": v(346.62, -287) * mm, "end": v(346.62, -317) * mm});
            skLineSegment(sketch, "E360", {"start": v(346.62, -317) * mm, "end": v(332.31, -317) * mm});
            skLineSegment(sketch, "E361", {"start": v(683.21, -200) * mm, "end": v(686.21, -200) * mm});
            skLineSegment(sketch, "E362", {"start": v(683.21, -160) * mm, "end": v(686.21, -160) * mm});
            skLineSegment(sketch, "E363", {"start": v(506.07, -160) * mm, "end": v(509.07, -160) * mm});
            skCircle(sketch, "E364", {"center": v(551.07, -133) * mm, "radius": 3 * mm});
            skCircle(sketch, "E365", {"center": v(641.21, -133) * mm, "radius": 3 * mm});
            skCircle(sketch, "E366", {"center": v(581.07, -133) * mm, "radius": 3 * mm});
            skCircle(sketch, "E367", {"center": v(611.21, -133) * mm, "radius": 3 * mm});
            skLineSegment(sketch, "E368", {"start": v(-783.36, -278) * mm, "end": v(-780.36, -278) * mm});
            skLineSegment(sketch, "E369", {"start": v(-780.36, -266) * mm, "end": v(-783.36, -266) * mm});
            skLineSegment(sketch, "E370", {"start": v(-783.36, -254.77) * mm, "end": v(-780.36, -254.77) * mm});
            skLineSegment(sketch, "E371", {"start": v(-780.36, -242.77) * mm, "end": v(-783.36, -242.77) * mm});
            skLineSegment(sketch, "E372", {"start": v(-783.36, -230.77) * mm, "end": v(-780.36, -230.77) * mm});
            skLineSegment(sketch, "E373", {"start": v(-780.36, -218.77) * mm, "end": v(-783.36, -218.77) * mm});
            skPoint(sketch, "E374.end.orphan", {"position": v(-780.36, -206.77) * mm});
            skLineSegment(sketch, "E375", {"start": v(-783.36, -206.77) * mm, "end": v(-780.36, -206.77) * mm});
            skLineSegment(sketch, "E376", {"start": v(-780.36, -194.77) * mm, "end": v(-783.36, -194.77) * mm});
            skLineSegment(sketch, "E377", {"start": v(-783.36, -182.77) * mm, "end": v(-780.36, -182.77) * mm});
            skLineSegment(sketch, "E378", {"start": v(-780.36, -170.77) * mm, "end": v(-783.36, -170.77) * mm});
            skLineSegment(sketch, "E379", {"start": v(-783.36, -158) * mm, "end": v(-780.36, -158) * mm});
            skLineSegment(sketch, "E380", {"start": v(-780.36, -146) * mm, "end": v(-783.36, -146) * mm});
            skLineSegment(sketch, "E381", {"start": v(-783.36, -134) * mm, "end": v(-780.36, -134) * mm});
            skLineSegment(sketch, "E382", {"start": v(-780.36, -122) * mm, "end": v(-783.36, -122) * mm});
            skLineSegment(sketch, "E383", {"start": v(-780.36, -122) * mm, "end": v(-780.36, -113.2) * mm});
            skLineSegment(sketch, "E384", {"start": v(-783.36, -134) * mm, "end": v(-783.36, -122) * mm});
            skLineSegment(sketch, "E385", {"start": v(-783.36, -146) * mm, "end": v(-783.36, -158) * mm});
            skLineSegment(sketch, "E386", {"start": v(-783.36, -206.77) * mm, "end": v(-783.36, -194.77) * mm});
            skLineSegment(sketch, "E387", {"start": v(-780.36, -134) * mm, "end": v(-780.36, -146) * mm});
            skLineSegment(sketch, "E388", {"start": v(-783.36, -218.77) * mm, "end": v(-783.36, -230.77) * mm});
            skLineSegment(sketch, "E389", {"start": v(-780.36, -230.77) * mm, "end": v(-780.36, -242.77) * mm});
            skLineSegment(sketch, "E390", {"start": v(-783.36, -242.77) * mm, "end": v(-783.36, -254.77) * mm});
            skLineSegment(sketch, "E391", {"start": v(-783.36, -266) * mm, "end": v(-783.36, -278) * mm});
            skLineSegment(sketch, "E392", {"start": v(-780.36, -278) * mm, "end": v(-780.36, -284.7) * mm});
            skLineSegment(sketch, "E393.trimOffspring", {"start": v(-780.36, -158) * mm, "end": v(-780.36, -170.77) * mm});
            skLineSegment(sketch, "E394.trimOffspring", {"start": v(-780.36, -182.77) * mm, "end": v(-780.36, -194.77) * mm});
            skLineSegment(sketch, "E395.trimOffspring", {"start": v(-783.36, -182.77) * mm, "end": v(-783.36, -170.77) * mm});
            skLineSegment(sketch, "E396.trimOffspring", {"start": v(-780.36, -206.77) * mm, "end": v(-780.36, -218.77) * mm});
            skLineSegment(sketch, "E397", {"start": v(-780.36, -254.77) * mm, "end": v(-780.36, -266) * mm});
            skLineSegment(sketch, "E398.bottom", {"start": v(-780.36, -113.2) * mm, "end": v(-768.36, -113.2) * mm});
            skLineSegment(sketch, "E398.top", {"start": v(-768.36, -110.2) * mm, "end": v(-738.36, -110.2) * mm});
            skLineSegment(sketch, "E399", {"start": v(-768.36, -110.2) * mm, "end": v(-768.36, -113.2) * mm});
            skLineSegment(sketch, "E400", {"start": v(-738.36, -110.2) * mm, "end": v(-738.36, -113.2) * mm});
            skLineSegment(sketch, "E401.trimOffspring", {"start": v(-738.36, -113.2) * mm, "end": v(-726.36, -113.2) * mm});
            skPoint(sketch, "E402.end.orphan", {"position": v(-726.36, -284.7) * mm});
            skLineSegment(sketch, "E403", {"start": v(-738.36, -290.7) * mm, "end": v(-768.36, -290.7) * mm});
            skLineSegment(sketch, "E404", {"start": v(-768.36, -287.7) * mm, "end": v(-768.36, -290.7) * mm});
            skLineSegment(sketch, "E405", {"start": v(-738.36, -287.7) * mm, "end": v(-738.36, -290.7) * mm});
            skLineSegment(sketch, "E406", {"start": v(-780.36, -287.7) * mm, "end": v(-780.36, -284.7) * mm});
            skLineSegment(sketch, "E407", {"start": v(-726.36, -284.7) * mm, "end": v(-726.36, -287.7) * mm});
            skLineSegment(sketch, "E408", {"start": v(-768.36, -287.7) * mm, "end": v(-780.36, -287.7) * mm});
            skLineSegment(sketch, "E409", {"start": v(-726.36, -287.7) * mm, "end": v(-738.36, -287.7) * mm});
            skPoint(sketch, "E410.orphan", {"position": v(-780.36, -290.7) * mm});
            skPoint(sketch, "E411.orphan", {"position": v(-726.36, -290.7) * mm});
            skLineSegment(sketch, "E412", {"start": v(-216.06, -565.77) * mm, "end": v(-216.06, -556.77) * mm});
            skLineSegment(sketch, "E413", {"start": v(-216.06, -544.77) * mm, "end": v(-216.06, -532.77) * mm});
            skLineSegment(sketch, "E414", {"start": v(-216.06, -520.77) * mm, "end": v(-216.06, -508.77) * mm});
            skLineSegment(sketch, "E415", {"start": v(-216.06, -496.77) * mm, "end": v(-216.06, -484.77) * mm});
            skLineSegment(sketch, "E416", {"start": v(-216.06, -472.77) * mm, "end": v(-216.06, -460.77) * mm});
            skLineSegment(sketch, "E417", {"start": v(-216.06, -448.77) * mm, "end": v(-216.06, -436.77) * mm});
            skLineSegment(sketch, "E418", {"start": v(-216.06, -424.77) * mm, "end": v(-216.06, -412.77) * mm});
            skLineSegment(sketch, "E419", {"start": v(-216.06, -400.77) * mm, "end": v(-216.06, -388.77) * mm});
            skLineSegment(sketch, "E420", {"start": v(-216.06, -400.77) * mm, "end": v(-219.06, -400.77) * mm});
            skLineSegment(sketch, "E421", {"start": v(-219.06, -400.77) * mm, "end": v(-219.06, -412.77) * mm});
            skLineSegment(sketch, "E422", {"start": v(-219.06, -412.77) * mm, "end": v(-216.06, -412.77) * mm});
            skLineSegment(sketch, "E423", {"start": v(-216.06, -424.77) * mm, "end": v(-219.06, -424.77) * mm});
            skLineSegment(sketch, "E424", {"start": v(-219.06, -424.77) * mm, "end": v(-219.06, -436.77) * mm});
            skLineSegment(sketch, "E425", {"start": v(-219.06, -436.77) * mm, "end": v(-216.06, -436.77) * mm});
            skLineSegment(sketch, "E426", {"start": v(-216.06, -448.77) * mm, "end": v(-219.06, -448.77) * mm});
            skLineSegment(sketch, "E427", {"start": v(-219.06, -448.77) * mm, "end": v(-219.06, -460.77) * mm});
            skLineSegment(sketch, "E428", {"start": v(-219.06, -460.77) * mm, "end": v(-216.06, -460.77) * mm});
            skLineSegment(sketch, "E429", {"start": v(-216.06, -472.77) * mm, "end": v(-219.06, -472.77) * mm});
            skLineSegment(sketch, "E430", {"start": v(-219.06, -472.77) * mm, "end": v(-219.06, -484.77) * mm});
            skLineSegment(sketch, "E431", {"start": v(-219.06, -484.77) * mm, "end": v(-216.06, -484.77) * mm});
            skLineSegment(sketch, "E432", {"start": v(-216.06, -496.77) * mm, "end": v(-219.06, -496.77) * mm});
            skLineSegment(sketch, "E433", {"start": v(-219.06, -496.77) * mm, "end": v(-219.06, -508.77) * mm});
            skLineSegment(sketch, "E434", {"start": v(-219.06, -508.77) * mm, "end": v(-216.06, -508.77) * mm});
            skLineSegment(sketch, "E435", {"start": v(-216.06, -520.77) * mm, "end": v(-219.06, -520.77) * mm});
            skPoint(sketch, "E435.endSnap0", {"position": v(-219.06, -502.77) * mm});
            skLineSegment(sketch, "E436", {"start": v(-219.06, -520.77) * mm, "end": v(-219.06, -532.77) * mm});
            skLineSegment(sketch, "E437", {"start": v(-219.06, -532.77) * mm, "end": v(-216.06, -532.77) * mm});
            skLineSegment(sketch, "E438", {"start": v(-216.06, -544.77) * mm, "end": v(-219.06, -544.77) * mm});
            skLineSegment(sketch, "E439", {"start": v(-219.06, -544.77) * mm, "end": v(-219.06, -556.77) * mm});
            skLineSegment(sketch, "E440", {"start": v(-219.06, -556.77) * mm, "end": v(-216.06, -556.77) * mm});
            skLineSegment(sketch, "E441", {"start": v(-88.06, -395.99) * mm, "end": v(-88.06, -395.99) * mm});
            skLineSegment(sketch, "E442", {"start": v(-19.06, -388.77) * mm, "end": v(-19.06, -453.77) * mm});
            skPoint(sketch, "E443.start.orphan", {"position": v(-230.06, -568.77) * mm});
            skLineSegment(sketch, "E444.left", {"start": v(-119.06, -388.77) * mm, "end": v(-119.06, -388.77) * mm});
            skLineSegment(sketch, "E444.right", {"start": v(-69.06, -388.77) * mm, "end": v(-69.06, -388.77) * mm});
            skLineSegment(sketch, "E445.left", {"start": v(-119.06, -568.77) * mm, "end": v(-119.06, -565.77) * mm});
            skLineSegment(sketch, "E445.right", {"start": v(-69.06, -568.77) * mm, "end": v(-69.06, -565.77) * mm});
            skLineSegment(sketch, "E446.bottom", {"start": v(-19.06, -453.77) * mm, "end": v(-22.06, -453.77) * mm});
            skLineSegment(sketch, "E446.top", {"start": v(-19.06, -503.77) * mm, "end": v(-22.06, -503.77) * mm});
            skLineSegment(sketch, "E446.right", {"start": v(-22.06, -453.77) * mm, "end": v(-22.06, -503.77) * mm});
            skLineSegment(sketch, "E447.left", {"start": v(-119.06, -388.77) * mm, "end": v(-119.06, -391.77) * mm});
            skLineSegment(sketch, "E447.right", {"start": v(-69.06, -388.77) * mm, "end": v(-69.06, -391.77) * mm});
            skLineSegment(sketch, "E448.trimOffspring", {"start": v(-19.06, -503.77) * mm, "end": v(-19.06, -565.77) * mm});
            skLineSegment(sketch, "E449", {"start": v(-119.06, -388.77) * mm, "end": v(-69.06, -388.77) * mm});
            skLineSegment(sketch, "E450", {"start": v(-119.06, -391.77) * mm, "end": v(-216.06, -391.77) * mm});
            skLineSegment(sketch, "E451", {"start": v(-69.06, -391.77) * mm, "end": v(-19.06, -391.77) * mm});
            skLineSegment(sketch, "E452", {"start": v(-119.06, -565.77) * mm, "end": v(-216.06, -565.77) * mm});
            skLineSegment(sketch, "E453", {"start": v(-69.06, -565.77) * mm, "end": v(-19.06, -565.77) * mm});
            skLineSegment(sketch, "E454", {"start": v(-119.06, -568.77) * mm, "end": v(-69.06, -568.77) * mm});
            skPoint(sketch, "E455.orphan", {"position": v(-19.06, -568.77) * mm});
            skLineSegment(sketch, "E456", {"start": v(31.62, -388.77) * mm, "end": v(31.62, -453.77) * mm});
            skLineSegment(sketch, "E457.bottom", {"start": v(31.62, -453.77) * mm, "end": v(28.62, -453.77) * mm});
            skLineSegment(sketch, "E457.top", {"start": v(31.62, -503.77) * mm, "end": v(28.62, -503.77) * mm});
            skLineSegment(sketch, "E457.right", {"start": v(28.62, -453.77) * mm, "end": v(28.62, -503.77) * mm});
            skLineSegment(sketch, "E458.trimOffspring", {"start": v(31.62, -503.77) * mm, "end": v(31.62, -562.77) * mm});
            skPoint(sketch, "E459.orphan", {"position": v(31.62, -565.77) * mm});
            skLineSegment(sketch, "E460", {"start": v(31.62, -565.77) * mm, "end": v(43.62, -565.77) * mm});
            skPoint(sketch, "E461.orphan", {"position": v(28.62, -565.77) * mm});
            skLineSegment(sketch, "E462.top", {"start": v(93.62, -568.77) * mm, "end": v(43.62, -568.77) * mm});
            skLineSegment(sketch, "E462.left", {"start": v(93.62, -565.77) * mm, "end": v(93.62, -568.77) * mm});
            skLineSegment(sketch, "E462.right", {"start": v(43.62, -565.77) * mm, "end": v(43.62, -568.77) * mm});
            skLineSegment(sketch, "E463.trimOffspring", {"start": v(93.62, -565.77) * mm, "end": v(158.62, -565.77) * mm});
            skLineSegment(sketch, "E464", {"start": v(43.62, -388.77) * mm, "end": v(93.62, -388.77) * mm});
            skLineSegment(sketch, "E465", {"start": v(108.62, -388.77) * mm, "end": v(108.62, -453.77) * mm});
            skLineSegment(sketch, "E466", {"start": v(108.62, -503.77) * mm, "end": v(108.62, -565.77) * mm});
            skLineSegment(sketch, "E467", {"start": v(108.62, -565.77) * mm, "end": v(93.62, -565.77) * mm});
            skLineSegment(sketch, "E468", {"start": v(31.62, -562.77) * mm, "end": v(31.62, -565.77) * mm});
            skLineSegment(sketch, "E469.left", {"start": v(31.62, -388.77) * mm, "end": v(31.62, -388.77) * mm});
            skLineSegment(sketch, "E469.right", {"start": v(108.62, -388.77) * mm, "end": v(108.62, -388.77) * mm});
            skLineSegment(sketch, "E470.bottom", {"start": v(93.62, -388.77) * mm, "end": v(43.62, -388.77) * mm});
            skLineSegment(sketch, "E470.top", {"start": v(93.62, -388.77) * mm, "end": v(43.62, -388.77) * mm});
            skLineSegment(sketch, "E471", {"start": v(31.62, -391.77) * mm, "end": v(43.62, -391.77) * mm});
            skLineSegment(sketch, "E472", {"start": v(93.62, -388.77) * mm, "end": v(93.62, -391.77) * mm});
            skLineSegment(sketch, "E473", {"start": v(43.62, -388.77) * mm, "end": v(43.62, -391.77) * mm});
            skLineSegment(sketch, "E474.trimOffspring", {"start": v(93.62, -391.77) * mm, "end": v(108.62, -391.77) * mm});
            skLineSegment(sketch, "E475.trimOffspring", {"start": v(43.62, -565.77) * mm, "end": v(31.62, -565.77) * mm});
            skLineSegment(sketch, "E476.bottom", {"start": v(111.62, -453.77) * mm, "end": v(108.62, -453.77) * mm});
            skLineSegment(sketch, "E476.top", {"start": v(111.62, -503.77) * mm, "end": v(108.62, -503.77) * mm});
            skLineSegment(sketch, "E476.right", {"start": v(111.62, -453.77) * mm, "end": v(111.62, -503.77) * mm});
            skPoint(sketch, "E477", {"position": v(70.12, -478.77) * mm});
            skCircle(sketch, "E478", {"center": v(70.12, -478.77) * mm, "radius": 30 * mm});
            skSolve(sketch);
        }
        {
            var Q0;
            Q0=makeQuery(id+"F0.imprint","IMPRINT",FACE,{"disambiguationData":[TD([[makeQuery(id+"F0.imprint","IMPRINT",EDGE,{"derivedFrom":sQuery(id+"F0.wireOp",EDGE,"hHuDfWjk-tMOa-BbPO-4a9n-nJEn1wAJkAZW")}),-1.0]])]});
            var Q1;
            Q1=makeQuery(id+"F0.imprint","IMPRINT",FACE,{"disambiguationData":[TD([[makeQuery(id+"F0.imprint","IMPRINT",EDGE,{"derivedFrom":sQuery(id+"F0.wireOp",EDGE,"a7936c38-f306-4503-9546-df24e7af2122")}),-1.0]])]});
            var Q2;
            Q2=makeQuery(id+"F0.imprint","IMPRINT",FACE,{"disambiguationData":[TD([[makeQuery(id+"F0.imprint","IMPRINT",EDGE,{"derivedFrom":sQuery(id+"F0.wireOp",EDGE,"mVLbgt2A-FCme-7s1i-mUxD-7JJBTt3IhOLu.bottom")}),1.0]])]});
            var Q3;
            Q3=makeQuery(id+"F0.imprint","IMPRINT",FACE,{"disambiguationData":[TD([[makeQuery(id+"F0.imprint","IMPRINT",EDGE,{"derivedFrom":sQuery(id+"F0.wireOp",EDGE,"E0")}),-1.0]])]});
            var Q4;
            Q4=makeQuery(id+"F0.imprint","IMPRINT",FACE,{"disambiguationData":[TD([[makeQuery(id+"F0.imprint","IMPRINT",EDGE,{"derivedFrom":sQuery(id+"F0.wireOp",EDGE,"E190.right")}),1.0]])]});
            var Q5;
            {var subQ5=sQuery(id+"F0.wireOp",EDGE,"E49.top");Q5=makeQuery(id+"F0.imprint","IMPRINT",FACE,{"disambiguationData":[TD([[makeQuery(id+"F0.imprint","IMPRINT",EDGE,{"derivedFrom":subQ5}),-1.0]])]});}
            var Q6;
            Q6=makeQuery(id+"F0.imprint","IMPRINT",FACE,{"disambiguationData":[TD([[makeQuery(id+"F0.imprint","IMPRINT",EDGE,{"derivedFrom":sQuery(id+"F0.wireOp",EDGE,"E250.top")}),-1.0]])]});
            var Q7;
            Q7=makeQuery(id+"F0.imprint","IMPRINT",FACE,{"disambiguationData":[TD([[makeQuery(id+"F0.imprint","IMPRINT",EDGE,{"derivedFrom":sQuery(id+"F0.wireOp",EDGE,"E231.MirrorCS")}),-1.0]])]});
            var Q8;
            Q8=makeQuery(id+"F0.imprint","IMPRINT",FACE,{"disambiguationData":[TD([[makeQuery(id+"F0.imprint","IMPRINT",EDGE,{"derivedFrom":sQuery(id+"F0.wireOp",EDGE,"e9bd65cd-c21d-4e1d-a616-8fcb1cedc9741.MirrorCS")}),1.0]])]});
            var Q9;
            Q9=makeQuery(id+"F0.imprint","IMPRINT",FACE,{"disambiguationData":[TD([[makeQuery(id+"F0.imprint","IMPRINT",EDGE,{"derivedFrom":sQuery(id+"F0.wireOp",EDGE,"E266.MirrorCS")}),1.0]])]});
            var Q10;
            Q10=makeQuery(id+"F0.imprint","IMPRINT",FACE,{"disambiguationData":[TD([[makeQuery(id+"F0.imprint","IMPRINT",EDGE,{"derivedFrom":sQuery(id+"F0.wireOp",EDGE,"E287")}),-1.0]])]});
            var Q11;
            Q11=makeQuery(id+"F0.imprint","IMPRINT",FACE,{"disambiguationData":[TD([[makeQuery(id+"F0.imprint","IMPRINT",EDGE,{"derivedFrom":sQuery(id+"F0.wireOp",EDGE,"E412")}),-1.0]])]});
            var Q12;
            {var subQ3=sQuery(id+"F0.wireOp",EDGE,"E457.bottom");Q12=makeQuery(id+"F0.imprint","IMPRINT",FACE,{"disambiguationData":[TD([[makeQuery(id+"F0.imprint","IMPRINT",EDGE,{"derivedFrom":subQ3}),1.0]])]});}
            extrude(context, id + "F1", {"entities" : qUnion([Q0, Q1, Q2, Q3, Q4, Q5, Q6, Q7, Q8, Q9, Q10, Q11, Q12]), "oppositeDirection" : true, "depth" : 3 * mm, "offsetDistance" : 25 * mm});
        }
        {
            var Q0;
            {var subQ14=sQuery(id+"F0.wireOp",EDGE,"E13.left");Q0=makeQuery(id+"F0.imprint","IMPRINT",FACE,{"disambiguationData":[TD([[makeQuery(id+"F0.imprint","IMPRINT",EDGE,{"derivedFrom":subQ14}),1.0]])]});}
            extrude(context, id + "F2", {"entities" : qUnion([Q0]), "oppositeDirection" : true, "depth" : 3 * mm, "offsetDistance" : 25 * mm});
        }
        {
            var Q0;
            Q0=qCreatedBy(makeId("Front.planeOp"),FACE);
            var sketch = newSketch(context, id + "F3", { "sketchPlane" : qUnion([Q0])});
            skCircle(sketch, "E479", {"center": v(-381.9, -139.01) * mm, "radius": 6.75 * mm});
            skCircle(sketch, "E480.0", {"center": v(-381.9, -139.01) * mm, "radius": 11.25 * mm});
            skLineSegment(sketch, "E481", {"start": v(-393.13, -138.56) * mm, "end": v(-388.63, -138.56) * mm});
            skCircle(sketch, "E482", {"center": v(-381.9, -131.01) * mm, "radius": 1 * mm});
            skCircle(sketch, "E483", {"center": v(-390.13, -142.64) * mm, "radius": 1 * mm});
            skCircle(sketch, "E484", {"center": v(-373.84, -143.03) * mm, "radius": 1 * mm});
            skCircle(sketch, "E485", {"center": v(-381.9, -139.01) * mm, "radius": 2.5 * mm});
            skLineSegment(sketch, "E486", {"start": v(-389.14, -147.61) * mm, "end": v(-391.9, -150.26) * mm});
            skLineSegment(sketch, "E487", {"start": v(-391.9, -150.26) * mm, "end": v(-381.9, -150.26) * mm});
            skLineSegment(sketch, "E488", {"start": v(-371.9, -150.26) * mm, "end": v(-374.64, -147.61) * mm});
            skLineSegment(sketch, "E489", {"start": v(-381.9, -150.26) * mm, "end": v(-371.9, -150.26) * mm});
            skPoint(sketch, "E490", {"position": v(-381.9, -150.26) * mm});
            skLineSegment(sketch, "E491", {"start": v(-375.14, -139.01) * mm, "end": v(-370.64, -139.01) * mm});
            skLineSegment(sketch, "E492", {"start": v(-370.64, -139.01) * mm, "end": v(-370.64, -120.01) * mm});
            skLineSegment(sketch, "E493", {"start": v(-371.64, -119.01) * mm, "end": v(-377.14, -119.01) * mm});
            skLineSegment(sketch, "E494", {"start": v(-378.14, -120.01) * mm, "end": v(-378.14, -128.4) * mm});
            skLineSegment(sketch, "E495", {"start": v(-370.64, -119.98) * mm, "end": v(-378.14, -119.98) * mm});
            skPoint(sketch, "E496.visualSharp", {"position": v(-370.64, -119.01) * mm});
            skArc(sketch, "E496.filletArc", {"start": v(-370.64, -120.01) * mm, "mid": v(-370.93, -119.3) * mm, "end": v(-371.64, -119.01) * mm});
            skPoint(sketch, "E497.visualSharp", {"position": v(-378.14, -119.01) * mm});
            skArc(sketch, "E497.filletArc", {"start": v(-377.14, -119.01) * mm, "mid": v(-377.85, -119.3) * mm, "end": v(-378.14, -120.01) * mm});
            skSolve(sketch);
        }
        {
            var Q0;
            Q0=makeQuery(id+"F3.imprint","IMPRINT",FACE,{"disambiguationData":[TD([[makeQuery(id+"F3.imprint","IMPRINT",EDGE,{"derivedFrom":sQuery(id+"F3.wireOp",EDGE,"E482")}),1.0]])]});
            var Q1;
            Q1=makeQuery(id+"F3.imprint","IMPRINT",FACE,{"disambiguationData":[TD([[makeQuery(id+"F3.imprint","IMPRINT",EDGE,{"derivedFrom":sQuery(id+"F3.wireOp",EDGE,"E484")}),1.0]])]});
            var Q2;
            Q2=makeQuery(id+"F3.imprint","IMPRINT",FACE,{"disambiguationData":[TD([[makeQuery(id+"F3.imprint","IMPRINT",EDGE,{"derivedFrom":sQuery(id+"F3.wireOp",EDGE,"E483")}),1.0]])]});
            extrude(context, id + "F4", {"entities" : qUnion([Q0, Q1, Q2]), "oppositeDirection" : true, "depth" : 2 * mm, "offsetDistance" : 25 * mm});
        }
        {
            var Q0;
            {var subQ5=sQuery(id+"F3.wireOp",EDGE,"hgsHxCeP-JT37-CoEv-zDdw-DwPJparBNKJz");Q0=makeQuery(id+"F3.imprint","IMPRINT",FACE,{"disambiguationData":[TD([[makeQuery(id+"F3.imprint","IMPRINT",EDGE,{"derivedFrom":subQ5}),1.0]])]});}
            var Q1;
            Q1=makeQuery(id+"F3.imprint","IMPRINT",FACE,{"disambiguationData":[TD([[makeQuery(id+"F3.imprint","IMPRINT",EDGE,{"derivedFrom":sQuery(id+"F3.wireOp",EDGE,"E485")}),-1.0]])]});
            var Q2;
            Q2=makeQuery(id+"F3.imprint","IMPRINT",FACE,{"disambiguationData":[TD([[makeQuery(id+"F3.imprint","IMPRINT",EDGE,{"derivedFrom":sQuery(id+"F3.wireOp",EDGE,"E485")}),1.0]])]});
            var Q3;
            {var subQ0=sQuery(id+"F3.wireOp",EDGE,"hgsHxCeP-JT37-CoEv-zDdw-DwPJparBNKJz");Q3=makeQuery(id+"F3.imprint","IMPRINT",FACE,{"disambiguationData":[TD([[makeQuery(id+"F3.imprint","IMPRINT",EDGE,{"derivedFrom":subQ0}),-1.0]])]});}
            var Q4;
            {var subQ0=sQuery(id+"F3.wireOp",EDGE,"E481");Q4=makeQuery(id+"F3.imprint","IMPRINT",FACE,{"disambiguationData":[TD([[makeQuery(id+"F3.imprint","IMPRINT",EDGE,{"derivedFrom":subQ0}),1.0]])]});}
            var Q5;
            {var subQ3=sQuery(id+"F3.wireOp",EDGE,"E481");Q5=makeQuery(id+"F3.imprint","IMPRINT",FACE,{"disambiguationData":[TD([[makeQuery(id+"F3.imprint","IMPRINT",EDGE,{"derivedFrom":subQ3}),-1.0]])]});}
            var Q6;
            Q6=makeQuery(id+"F4.opExtrude","CAP_FACE",FACE,{"disambiguationData":[OSD([sQuery(id+"F3.wireOp",EDGE,"E484")])],"isStart":false});
            var Q7;
            Q7=makeQuery(id+"F4.opExtrude","CAP_FACE",FACE,{"disambiguationData":[OSD([sQuery(id+"F3.wireOp",EDGE,"E482")])],"isStart":false});
            var Q8;
            Q8=makeQuery(id+"F4.opExtrude","CAP_FACE",FACE,{"disambiguationData":[OSD([sQuery(id+"F3.wireOp",EDGE,"E483")])],"isStart":false});
            extrude(context, id + "F5", {"entities" : qUnion([Q0, Q1, Q2, Q3, Q4, Q5, Q6, Q7, Q8]), "depth" : 42 * mm, "offsetDistance" : 25 * mm});
        }
        {
            var Q0;
            Q0=makeQuery(id+"F3.imprint","IMPRINT",FACE,{"disambiguationData":[TD([[makeQuery(id+"F3.imprint","IMPRINT",EDGE,{"derivedFrom":sQuery(id+"F3.wireOp",EDGE,"E485")}),-1.0]])]});
            extrude(context, id + "F6", {"entities" : qUnion([Q0]), "operationType" : NewBodyOperationType.ADD, "oppositeDirection" : true, "depth" : 1 * mm, "offsetDistance" : 25 * mm});
        }
        {
            var Q0;
            {var subQ2=sQuery(id+"F3.wireOp",EDGE,"E488");Q0=makeQuery(id+"F3.imprint","IMPRINT",FACE,{"disambiguationData":[TD([[makeQuery(id+"F3.imprint","IMPRINT",EDGE,{"derivedFrom":subQ2}),1.0]])]});}
            var Q1;
            {var subQ0=sQuery(id+"F3.wireOp",EDGE,"E486");Q1=makeQuery(id+"F3.imprint","IMPRINT",FACE,{"disambiguationData":[TD([[makeQuery(id+"F3.imprint","IMPRINT",EDGE,{"derivedFrom":subQ0}),1.0]])]});}
            extrude(context, id + "F7", {"entities" : qUnion([Q0, Q1]), "operationType" : NewBodyOperationType.ADD, "depth" : 27.5 * mm, "offsetDistance" : 25 * mm});
        }
        {
            var Q0;
            {var subQ0=sQuery(id+"F3.wireOp",EDGE,"E486");Q0=makeQuery(id+"F3.imprint","IMPRINT",FACE,{"disambiguationData":[TD([[makeQuery(id+"F3.imprint","IMPRINT",EDGE,{"derivedFrom":subQ0}),1.0]])]});}
            var Q1;
            {var subQ2=sQuery(id+"F3.wireOp",EDGE,"E488");Q1=makeQuery(id+"F3.imprint","IMPRINT",FACE,{"disambiguationData":[TD([[makeQuery(id+"F3.imprint","IMPRINT",EDGE,{"derivedFrom":subQ2}),1.0]])]});}
            extrude(context, id + "F8", {"entities" : qUnion([Q0, Q1]), "operationType" : NewBodyOperationType.REMOVE, "depth" : 10 * mm, "offsetDistance" : 25 * mm});
        }
        {
            var Q0;
            Q0=makeQuery(id+"F5.opExtrude","CAP_FACE",FACE,{"disambiguationData":[OSD([sQuery(id+"F3.wireOp",EDGE,"E480.0")])],"isStart":false});
            var sketch = newSketch(context, id + "F9", { "sketchPlane" : qUnion([Q0])});
            skCircle(sketch, "E498", {"center": v(-384.07, -142.55) * mm, "radius": 2.5 * mm});
            skLineSegment(sketch, "E499", {"start": v(-384.07, -142.55) * mm, "end": v(-392.57, -142.55) * mm, "construction": true});
            skLineSegment(sketch, "E500", {"start": v(-392.57, -142.55) * mm, "end": v(-384.07, -142.55) * mm});
            skLineSegment(sketch, "E501", {"start": v(-384.07, -142.55) * mm, "end": v(-384.07, -150.05) * mm, "construction": true});
            skCircle(sketch, "E502.0", {"center": v(-384.07, -142.55) * mm, "radius": 1.5 * mm});
            skSolve(sketch);
        }
        {
            var Q0;
            Q0=makeQuery(id+"F9.imprint","IMPRINT",FACE,{"disambiguationData":[TD([[makeQuery(id+"F9.imprint","IMPRINT",EDGE,{"derivedFrom":sQuery(id+"F9.wireOp",EDGE,"E498")}),1.0]])]});
            extrude(context, id + "F10", {"entities" : qUnion([Q0]), "operationType" : NewBodyOperationType.ADD, "depth" : 1 * mm, "offsetDistance" : 25 * mm});
        }
        {
            var Q0;
            Q0=qCreatedBy(makeId("Front.planeOp"),FACE);
            var sketch = newSketch(context, id + "F11", { "sketchPlane" : qUnion([Q0])});
            skCircle(sketch, "E503", {"center": v(-416.66, -138.62) * mm, "radius": 6.75 * mm});
            skCircle(sketch, "E504.0", {"center": v(-416.66, -138.62) * mm, "radius": 11.25 * mm});
            skLineSegment(sketch, "E505", {"start": v(-427.9, -138.17) * mm, "end": v(-423.4, -138.17) * mm});
            skCircle(sketch, "E506", {"center": v(-416.66, -129.62) * mm, "radius": 1 * mm});
            skCircle(sketch, "E507", {"center": v(-424.9, -142.26) * mm, "radius": 1 * mm});
            skCircle(sketch, "E508", {"center": v(-408.6, -142.64) * mm, "radius": 1 * mm});
            skCircle(sketch, "E509", {"center": v(-416.66, -138.62) * mm, "radius": 2.5 * mm});
            skPoint(sketch, "E510", {"position": v(-416.66, -149.87) * mm});
            skLineSegment(sketch, "E511", {"start": v(-409.91, -138.62) * mm, "end": v(-405.41, -138.62) * mm});
            skLineSegment(sketch, "E512", {"start": v(-405.41, -138.62) * mm, "end": v(-405.41, -119.62) * mm});
            skLineSegment(sketch, "E513", {"start": v(-406.41, -118.62) * mm, "end": v(-411.91, -118.62) * mm});
            skLineSegment(sketch, "E514", {"start": v(-412.91, -119.62) * mm, "end": v(-412.91, -128.02) * mm});
            skLineSegment(sketch, "E515", {"start": v(-405.41, -119.6) * mm, "end": v(-412.91, -119.6) * mm});
            skPoint(sketch, "E516.visualSharp", {"position": v(-405.41, -118.62) * mm});
            skArc(sketch, "E516.filletArc", {"start": v(-405.41, -119.62) * mm, "mid": v(-405.7, -118.92) * mm, "end": v(-406.41, -118.62) * mm});
            skPoint(sketch, "E517.visualSharp", {"position": v(-412.91, -118.62) * mm});
            skArc(sketch, "E517.filletArc", {"start": v(-411.91, -118.62) * mm, "mid": v(-412.62, -118.92) * mm, "end": v(-412.91, -119.62) * mm});
            skCircle(sketch, "E518.0", {"center": v(-416.66, -138.62) * mm, "radius": 10.25 * mm});
            skCircle(sketch, "E519.0", {"center": v(-416.66, -138.62) * mm, "radius": 3.5 * mm});
            skSolve(sketch);
        }
        {
            var Q0;
            {var subQ1=sQuery(id+"F11.wireOp",EDGE,"E504.0");var subQ5=sQuery(id+"F11.wireOp",EDGE,"E505");var subQ6=makeQuery(id+"F11.imprint","INTERSECT",VERTEX,{"derivedFrom":[subQ1,subQ5]});Q0=makeQuery(id+"F11.imprint","IMPRINT",FACE,{"disambiguationData":[TD([[makeQuery(id+"F11.imprint","IMPRINT",EDGE,{"disambiguationData":[TD([[subQ6,1.0]])],"derivedFrom":subQ1}),1.0]])]});}
            var Q1;
            Q1=makeQuery(id+"F11.imprint","IMPRINT",FACE,{"disambiguationData":[TD([[makeQuery(id+"F11.imprint","IMPRINT",EDGE,{"derivedFrom":sQuery(id+"F11.wireOp",EDGE,"E507")}),-1.0]])]});
            var Q2;
            Q2=makeQuery(id+"F11.imprint","IMPRINT",FACE,{"disambiguationData":[TD([[makeQuery(id+"F11.imprint","IMPRINT",EDGE,{"derivedFrom":sQuery(id+"F11.wireOp",EDGE,"E506")}),-1.0]])]});
            var Q3;
            Q3=makeQuery(id+"F11.imprint","IMPRINT",FACE,{"disambiguationData":[TD([[makeQuery(id+"F11.imprint","IMPRINT",EDGE,{"derivedFrom":sQuery(id+"F11.wireOp",EDGE,"E506")}),1.0]])]});
            var Q4;
            Q4=makeQuery(id+"F11.imprint","IMPRINT",FACE,{"disambiguationData":[TD([[makeQuery(id+"F11.imprint","IMPRINT",EDGE,{"derivedFrom":sQuery(id+"F11.wireOp",EDGE,"E508")}),1.0]])]});
            var Q5;
            Q5=makeQuery(id+"F11.imprint","IMPRINT",FACE,{"disambiguationData":[TD([[makeQuery(id+"F11.imprint","IMPRINT",EDGE,{"derivedFrom":sQuery(id+"F11.wireOp",EDGE,"E507")}),1.0]])]});
            var Q6;
            {var subQ0=sQuery(id+"F11.wireOp",EDGE,"E504.0");var subQ5=sQuery(id+"F11.wireOp",EDGE,"E505");var subQ10=makeQuery(id+"F11.imprint","INTERSECT",VERTEX,{"derivedFrom":[subQ0,subQ5]});Q6=makeQuery(id+"F11.imprint","IMPRINT",FACE,{"disambiguationData":[TD([[makeQuery(id+"F11.imprint","IMPRINT",EDGE,{"disambiguationData":[TD([[subQ10,-1.0]])],"derivedFrom":subQ0}),1.0]])]});}
            var Q7;
            Q7=makeQuery(id+"F11.imprint","IMPRINT",FACE,{"disambiguationData":[TD([[makeQuery(id+"F11.imprint","IMPRINT",EDGE,{"derivedFrom":sQuery(id+"F11.wireOp",EDGE,"E519.0")}),-1.0]])]});
            extrude(context, id + "F12", {"entities" : qUnion([Q0, Q1, Q2, Q3, Q4, Q5, Q6, Q7]), "depth" : 10 * mm, "offsetDistance" : 25 * mm});
        }
        {
            var Q0;
            Q0=makeQuery(id+"F11.imprint","IMPRINT",FACE,{"disambiguationData":[TD([[makeQuery(id+"F11.imprint","IMPRINT",EDGE,{"derivedFrom":sQuery(id+"F11.wireOp",EDGE,"E506")}),1.0]])]});
            var Q1;
            Q1=makeQuery(id+"F11.imprint","IMPRINT",FACE,{"disambiguationData":[TD([[makeQuery(id+"F11.imprint","IMPRINT",EDGE,{"derivedFrom":sQuery(id+"F11.wireOp",EDGE,"E507")}),1.0]])]});
            var Q2;
            Q2=makeQuery(id+"F11.imprint","IMPRINT",FACE,{"disambiguationData":[TD([[makeQuery(id+"F11.imprint","IMPRINT",EDGE,{"derivedFrom":sQuery(id+"F11.wireOp",EDGE,"E508")}),1.0]])]});
            extrude(context, id + "F13", {"entities" : qUnion([Q0, Q1, Q2]), "operationType" : NewBodyOperationType.REMOVE, "depth" : 2 * mm, "offsetDistance" : 25 * mm});
        }
        {
            var Q0;
            Q0=makeQuery(id+"F11.imprint","IMPRINT",FACE,{"disambiguationData":[TD([[makeQuery(id+"F11.imprint","IMPRINT",EDGE,{"derivedFrom":sQuery(id+"F11.wireOp",EDGE,"E509")}),-1.0]])]});
            extrude(context, id + "F14", {"entities" : qUnion([Q0]), "operationType" : NewBodyOperationType.ADD, "depth" : 15 * mm, "offsetDistance" : 25 * mm});
        }
        {
            var Q0;
            Q0=makeQuery(id+"F11.imprint","IMPRINT",FACE,{"disambiguationData":[TD([[makeQuery(id+"F11.imprint","IMPRINT",EDGE,{"derivedFrom":sQuery(id+"F11.wireOp",EDGE,"E519.0")}),-1.0]])]});
            var Q1;
            Q1=makeQuery(id+"F11.imprint","IMPRINT",FACE,{"disambiguationData":[TD([[makeQuery(id+"F11.imprint","IMPRINT",EDGE,{"derivedFrom":sQuery(id+"F11.wireOp",EDGE,"E509")}),-1.0]])]});
            extrude(context, id + "F15", {"entities" : qUnion([Q0, Q1]), "operationType" : NewBodyOperationType.REMOVE, "depth" : 1.5 * mm, "offsetDistance" : 25 * mm});
        }
        {
            var Q0;
            Q0=makeQuery(id+"F14.opExtrude","CAP_EDGE",EDGE,{"disambiguationData":[OSD([sQuery(id+"F11.wireOp",EDGE,"E519.0")])],"isStart":false});
            chamfer(context, id + "F16", {"entities" : qUnion([Q0]), "width" : 0.5 * mm, "tangentPropagation" : true});
        }
    });
